FCSTD DOCUMENT  (FreeCAD 1.1R38827 (Git))
Label: composit_stand3_base_part_assembly
License: All rights reserved
LicenseURL: http://en.wikipedia.org/wiki/All_rights_reserved
objects: App::Link×16, PartDesign::CoordinateSystem×3, App::DocumentObjectGroup×3, Part::FeaturePython×3, App::Part×2, App::FeaturePython×1
note: 6 computed .brp shape members not serialized (recipe doc carries the construction recipe); baked Part::Feature solids carry a one-line shape summary decoded from their .brp
EXTERNAL_REF file=composit_stand3_base_part2_model.FCStd obj=Local_CS
EXTERNAL_REF file=composit_stand3_base_part2_model.FCStd obj=Body
EXTERNAL_REF file=composit_stand3_base_part2_model.FCStd obj=Local_CS001
EXTERNAL_REF file=composit_stand3_sink_assembly.FCStd obj=LCS_Origin
EXTERNAL_REF file=composit_stand3_sink_assembly.FCStd obj=Assembly
EXTERNAL_REF file=composit_stand3_base_part2_model.FCStd obj=Local_CS002
EXTERNAL_REF file=composit_stand3_base_part2_model.FCStd obj=Local_CS003
EXTERNAL_REF file=composit_stand3_base_part1_model.FCStd obj=Local_CS
EXTERNAL_REF file=composit_stand3_base_part1_model.FCStd obj=Body
EXTERNAL_REF file=composit_stand3_bottom_shield_model.FCStd obj=Local_CS
EXTERNAL_REF file=composit_stand3_bottom_shield_model.FCStd obj=Body
EXTERNAL_REF file=composit_stand3_base_part1_main.FCStd obj=Join
EXTERNAL_REF file=../module.FCStd obj=Body
EXTERNAL_REF file=composit_stand3_base_part1_model.FCStd obj=Local_CS001
EXTERNAL_REF file=composit_stand3_dropper_fix_assembly.FCStd obj=LCS_Origin
EXTERNAL_REF file=composit_stand3_dropper_fix_assembly.FCStd obj=Assembly
EXTERNAL_REF file=composit_stand3_base_part2_model.FCStd obj=Local_CS004
EXTERNAL_REF file=composit_stand3_base_part2_model.FCStd obj=Local_CS005
EXTERNAL_REF file=composit_stand3_base_part1_main.FCStd obj=Placment
EXTERNAL_REF file=composit_stand3_base_part2_model.FCStd obj=Local_CS006
EXTERNAL_REF file=composit_stand3_top_amplifier_model.FCStd obj=Local_CS
EXTERNAL_REF file=composit_stand3_top_amplifier_model.FCStd obj=Body
EXTERNAL_REF file=composit_stand3_base_part2_model.FCStd obj=Local_CS007
EXTERNAL_REF file=composit_stand3_base_part2_model.FCStd obj=Local_CS008

FEATURE [PartDesign::CoordinateSystem] LCS_Origin
  AttacherType = Attacher::AttachEngine3D
  AttachmentSupport = -> [X_Axis]
  MapMode = 2
FEATURE [App::DocumentObjectGroup] Constraints
FEATURE [App::FeaturePython] Variables  # WARN: FeaturePython — macro-defined, semantics opaque (R4)
  Type = App::PropertyContainer
FEATURE [App::DocumentObjectGroup] Configurations
FEATURE [App::Link] part2
  AttachedBy = #Local_CS
  AttachedTo = Parent Assembly#LCS_Origin
  AttachmentOffset = pos=(0,0,0) rot=(0,0,1;2.0944rad)
  LinkPlacement = pos=(0,0,0) rot=(0,0,1;2.0944rad)
  LinkedObject = -> <external composit_stand3_base_part2_model.FCStd>#Body
  Placement = pos=(0,0,0) rot=(0,0,1;2.0944rad)
  SolverId = Asm4EE
  expr: Placement = LCS_Origin.Placement * AttachmentOffset * composit_stand3_base_part2_model#Local_CS.Placement ^ -1
FEATURE [App::Link] composit_stand3_sink_assembly
  AttachedBy = #LCS_Origin
  AttachedTo = part2#Local_CS001
  LinkPlacement = pos=(-16.7432,7.1e-15,410) rot=(0,0,1;3.14159rad)
  LinkedObject = -> <external composit_stand3_sink_assembly.FCStd>#Assembly
  Placement = pos=(-16.7432,7.1e-15,410) rot=(0,0,1;3.14159rad)
  SolverId = Asm4EE
  expr: Placement = part2.Placement * composit_stand3_base_part2_model#Local_CS001.Placement * AttachmentOffset * composit_stand3_sink_assembly#LCS_Origin.Placement ^ -1
FEATURE [App::Link] composit_stand3_sink_assembly001
  AttachedBy = #LCS_Origin
  AttachedTo = part2#Local_CS002
  LinkPlacement = pos=(8.37158,-14.5,410) rot=(0,0,1;5.23599rad)
  LinkedObject = -> <external composit_stand3_sink_assembly.FCStd>#Assembly
  Placement = pos=(8.37158,-14.5,410) rot=(0,0,1;5.23599rad)
  SolverId = Asm4EE
  expr: Placement = part2.Placement * composit_stand3_base_part2_model#Local_CS002.Placement * AttachmentOffset * composit_stand3_sink_assembly#LCS_Origin.Placement ^ -1
FEATURE [App::Link] composit_stand3_sink_assembly002
  AttachedBy = #LCS_Origin
  AttachedTo = part2#Local_CS003
  LinkPlacement = pos=(8.37158,14.5,410) rot=(0,0,-1;5.23599rad)
  LinkedObject = -> <external composit_stand3_sink_assembly.FCStd>#Assembly
  Placement = pos=(8.37158,14.5,410) rot=(0,0,-1;5.23599rad)
  SolverId = Asm4EE
  expr: Placement = part2.Placement * composit_stand3_base_part2_model#Local_CS003.Placement * AttachmentOffset * composit_stand3_sink_assembly#LCS_Origin.Placement ^ -1
FEATURE [App::Link] part1
  AttachedBy = #Local_CS
  AttachedTo = Parent Assembly#LCS_Origin
  LinkedObject = -> <external composit_stand3_base_part1_model.FCStd>#Body
  SolverId = Asm4EE
  expr: Placement = LCS_Origin.Placement * AttachmentOffset * composit_stand3_base_part1_model#Local_CS.Placement ^ -1
FEATURE [App::Link] bottom_shield
  AttachedBy = #Local_CS
  AttachedTo = Parent Assembly#LCS_Origin
  AttachmentOffset = pos=(0,0,0) rot=(0,0,1;3.14159rad)
  LinkPlacement = pos=(0,0,0) rot=(0,0,1;3.14159rad)
  LinkedObject = -> <external composit_stand3_bottom_shield_model.FCStd>#Body
  Placement = pos=(0,0,0) rot=(0,0,1;3.14159rad)
  SolverId = Asm4EE
  expr: Placement = LCS_Origin.Placement * AttachmentOffset * composit_stand3_bottom_shield_model#Local_CS.Placement ^ -1
FEATURE [App::Link] bottom_shield001
  AttachedBy = #Local_CS
  AttachedTo = Parent Assembly#LCS_Origin
  AttachmentOffset = pos=(0,0,0) rot=(0,0,1;1.0472rad)
  LinkPlacement = pos=(0,0,0) rot=(0,0,1;1.0472rad)
  LinkedObject = -> <external composit_stand3_bottom_shield_model.FCStd>#Body
  Placement = pos=(0,0,0) rot=(0,0,1;1.0472rad)
  SolverId = Asm4EE
  expr: Placement = LCS_Origin.Placement * AttachmentOffset * composit_stand3_bottom_shield_model#Local_CS.Placement ^ -1
FEATURE [App::Link] Link  label="modules_placements"
  LinkedObject = -> <external composit_stand3_base_part1_main.FCStd>#Join
FEATURE [Part::FeaturePython] PolarArray  # WARN: FeaturePython — macro-defined, semantics opaque (R4)
  Alignment = 0
  AttacherType = Attacher::AttachEngine3D
  CellStart = A1
  Count = 3
  DistributionLaw = 0
  EndInclusive = false
  ExposePlacement = false
  FlipX = false
  FlipZ = false
  GeneratorMode = 0
  MarkerShape = 1
  MarkerSize = 200
  NumElements = 3
  OrientMode = 2
  Radius = 0
  Reverse = false
  SpanEnd = 360
  SpanStart = 0
  Step = 120
  Type = lattice2PolarArray2.PolarArray
  UseArcRadius = false
  UseArcRange = 0
  VSGVersion = 1
  Values = 0.0 | 120.0 | 240.0
  ValuesSource = 2
  isLattice = 1
FEATURE [Part::FeaturePython] Populate  label="Populate PolarArray with modules_placements"  # WARN: FeaturePython — macro-defined, semantics opaque (R4)
  Copying = 0
  ExposePlacement = false
  MarkerShape = 1
  MarkerSize = 0
  NumElements = 132
  Object = -> Link
  OutputCompounding = 0
  PlacementsTo = -> PolarArray
  Referencing = 0
  Type = lattice2PopulateCopies.LatticePopulateCopies
  isLattice = 1
FEATURE [App::Link] Link001  label="module_Body"
  LinkedObject = -> <external ../module.FCStd>#Body
FEATURE [Part::FeaturePython] Populate001  label="Populate Populate PolarArray with modules_placements with module_Body"  # WARN: FeaturePython — macro-defined, semantics opaque (R4)
  Copying = 0
  ExposePlacement = false
  MarkerShape = 1
  MarkerSize = 0
  NumElements = 0
  Object = -> Link001
  OutputCompounding = 1
  PlacementsTo = -> Populate
  Referencing = 0
  Type = lattice2PopulateCopies.LatticePopulateCopies
  isLattice = 0
FEATURE [PartDesign::CoordinateSystem] LCS_Origin001
  AttacherType = Attacher::AttachEngine3D
  AttachmentSupport = -> [X_Axis001]
  MapMode = 2
FEATURE [App::Part] Part  label="modules"
  Group = -> [LCS_Origin001,PolarArray,Link001,Link,Populate,Populate001]
  Origin = -> Origin001
FEATURE [App::DocumentObjectGroup] Parts
  Group = -> [Part]
FEATURE [App::Link] modules  label="modules001"
  AttachedBy = #LCS_Origin001
  AttachedTo = Parent Assembly#LCS_Origin
  LinkedObject = -> Part
  SolverId = Asm4EE
  expr: Placement = LCS_Origin.Placement * AttachmentOffset * LCS_Origin001.Placement ^ -1
FEATURE [App::Link] composit_stand3_dropper_fix_assembly
  AttachedBy = #LCS_Origin
  AttachedTo = part1#Local_CS001
  LinkPlacement = pos=(0,0,1428) rot=(0,0,1;0rad)
  LinkedObject = -> <external composit_stand3_dropper_fix_assembly.FCStd>#Assembly
  Placement = pos=(0,0,1428) rot=(0,0,1;0rad)
  SolverId = Asm4EE
  expr: Placement = part1.Placement * composit_stand3_base_part1_model#Local_CS001.Placement * AttachmentOffset * composit_stand3_dropper_fix_assembly#LCS_Origin.Placement ^ -1
FEATURE [App::Link] composit_stand3_dropper_fix_assembly001
  AttachedBy = #LCS_Origin
  AttachedTo = part2#Local_CS004
  LinkPlacement = pos=(0,0,1428) rot=(0,0,1;2.0944rad)
  LinkedObject = -> <external composit_stand3_dropper_fix_assembly.FCStd>#Assembly
  Placement = pos=(0,0,1428) rot=(0,0,1;2.0944rad)
  SolverId = Asm4EE
  expr: Placement = part2.Placement * composit_stand3_base_part2_model#Local_CS004.Placement * AttachmentOffset * composit_stand3_dropper_fix_assembly#LCS_Origin.Placement ^ -1
FEATURE [App::Link] composit_stand3_dropper_fix_1  label="composit_stand3_dropper_fix_assembly002"
  AttachedBy = #LCS_Origin
  AttachedTo = part2#Local_CS005
  LinkPlacement = pos=(0,0,1428) rot=(0,0,1;4.18879rad)
  LinkedObject = -> <external composit_stand3_dropper_fix_assembly.FCStd>#Assembly
  Placement = pos=(0,0,1428) rot=(0,0,1;4.18879rad)
  SolverId = Asm4EE
  expr: Placement = part2.Placement * composit_stand3_base_part2_model#Local_CS005.Placement * AttachmentOffset * composit_stand3_dropper_fix_assembly#LCS_Origin.Placement ^ -1
FEATURE [PartDesign::CoordinateSystem] top_LCS
  AttacherType = Attacher::AttachEngine3D
  AttachmentOffset = pos=(0,0,1434) rot=(0,0,1;0rad)
  AttachmentSupport = -> [XY_Plane]
  MapMode = 5
  Placement = pos=(0,0,1434) rot=(0,0,1;0rad)
  expr: .AttachmentOffset.Base.z = <<composit_stand3_base_part1_main>>#<<top_placement>>.Placement.Base.z + 6 mm
FEATURE [App::Link] top_amplifier
  AttachedBy = #Local_CS
  AttachedTo = part2#Local_CS006
  LinkPlacement = pos=(-13.2791,6.2e-15,1428) rot=(0,0,1;3.14159rad)
  LinkedObject = -> <external composit_stand3_top_amplifier_model.FCStd>#Body
  Placement = pos=(-13.2791,6.2e-15,1428) rot=(0,0,1;3.14159rad)
  SolverId = Asm4EE
  expr: Placement = part2.Placement * composit_stand3_base_part2_model#Local_CS006.Placement * AttachmentOffset * composit_stand3_top_amplifier_model#Local_CS.Placement ^ -1
FEATURE [App::Link] top_amplifier_2
  AttachedBy = #Local_CS
  AttachedTo = part2#Local_CS007
  LinkPlacement = pos=(6.63953,-11.5,1428) rot=(0,0,1;5.23599rad)
  LinkedObject = -> <external composit_stand3_top_amplifier_model.FCStd>#Body
  Placement = pos=(6.63953,-11.5,1428) rot=(0,0,1;5.23599rad)
  SolverId = Asm4EE
  expr: Placement = part2.Placement * composit_stand3_base_part2_model#Local_CS007.Placement * AttachmentOffset * composit_stand3_top_amplifier_model#Local_CS.Placement ^ -1
FEATURE [App::Link] top_amplifier_1
  AttachedBy = #Local_CS
  AttachedTo = part2#Local_CS008
  LinkPlacement = pos=(6.63953,11.5,1428) rot=(0,0,-1;5.23599rad)
  LinkedObject = -> <external composit_stand3_top_amplifier_model.FCStd>#Body
  Placement = pos=(6.63953,11.5,1428) rot=(0,0,-1;5.23599rad)
  SolverId = Asm4EE
  expr: Placement = part2.Placement * composit_stand3_base_part2_model#Local_CS008.Placement * AttachmentOffset * composit_stand3_top_amplifier_model#Local_CS.Placement ^ -1
FEATURE [App::Part] Assembly
  AssemblyType = Part::Link
  Group = -> [LCS_Origin,Constraints,Variables,Configurations,part2,composit_stand3_sink_assembly,composit_stand3_sink_assembly001,composit_stand3_sink_assembly002,part1,bottom_shield,bottom_shield001,modules,composit_stand3_dropper_fix_assembly,composit_stand3_dropper_fix_assembly001,composit_stand3_dropper_fix_1,top_LCS,top_amplifier,top_amplifier_2,top_amplifier_1]
  Origin = -> Origin
  Type = Assembly

RESOLVED EXTERNAL PARTS (link-assembly join: the EXTERNAL_REF files above that resolve inside this repo's crawl, each included once):
---- part ../module.FCStd = doc fcstd_3955753b3a20 ----
FCSTD DOCUMENT  (FreeCAD 1.1R38827 (Git))
Label: module
License: All rights reserved
LicenseURL: http://en.wikipedia.org/wiki/All_rights_reserved
objects: Sketcher::SketchObject×2, Part::Feature×1, PartDesign::FeatureBase×1, PartDesign::Body×1, Spreadsheet::Sheet×1
note: 8 computed .brp shape members not serialized (recipe doc carries the construction recipe); baked Part::Feature solids carry a one-line shape summary decoded from their .brp

FEATURE [Part::Feature] Part__Feature  label="module002"
  shape: bbox 170 x 148 x 41.12 mm, 715 faces (baked)
FEATURE [Sketcher::SketchObject] Sketch  label="module_holes"
  ArcFitTolerance = 0
  FullyConstrained = true
  MakeInternals = false
  sketch-geometry (10):
    g0: LineSegment StartX=59.5 StartY=-3.5 StartZ=0 EndX=59.5 EndY=3.5 EndZ=0
    g1: LineSegment StartX=59.5 StartY=3.5 StartZ=0 EndX=72.5 EndY=3.5 EndZ=0
    g2: LineSegment StartX=72.5 StartY=3.5 StartZ=0 EndX=72.5 EndY=-3.5 EndZ=0
    g3: LineSegment StartX=72.5 StartY=-3.5 StartZ=0 EndX=59.5 EndY=-3.5 EndZ=0
    g4: GeomPoint [constr] X=66 Y=0 Z=0
    g5: LineSegment StartX=-72.5 StartY=-3.5 StartZ=0 EndX=-72.5 EndY=3.5 EndZ=0
    g6: LineSegment StartX=-72.5 StartY=3.5 StartZ=0 EndX=-59.5 EndY=3.5 EndZ=0
    g7: LineSegment StartX=-59.5 StartY=3.5 StartZ=0 EndX=-59.5 EndY=-3.5 EndZ=0
    g8: LineSegment StartX=-59.5 StartY=-3.5 StartZ=0 EndX=-72.5 EndY=-3.5 EndZ=0
    g9: GeomPoint [constr] X=-66 Y=0 Z=0
  constraints (25):
    c: Coincident(g0,g1)
    c: Coincident(g1,g2)
    c: Coincident(g2,g3)
    c: Coincident(g3,g0)
    c: Horizontal(g1)
    c: Horizontal(g3)
    c: Vertical(g0)
    c: Vertical(g2)
    c: Symmetric(g1,g0,g4)
    c: PointOnObject(g4,g-1)
    c: Coincident(g5,g6)
    c: Coincident(g6,g7)
    c: Coincident(g7,g8)
    c: Coincident(g8,g5)
    c: Horizontal(g6)
    c: Horizontal(g8)
    c: Vertical(g5)
    c: Vertical(g7)
    c: Symmetric(g6,g5,g9)
    c: Symmetric(g9,g4,g-2)
    c: Equal(g1,g6)
    c: Equal(g7,g2)
    c: DistanceX(g1,g1) = 13
    c: DistanceY(g2,g2) = 7
    c: DistanceX(g9,g4) = 132
FEATURE [PartDesign::FeatureBase] BaseFeature
  BaseFeature = -> Part__Feature
  Placement = pos=(0,0,0) rot=(0,0,1;1.5708rad)
  Suppressed = false
FEATURE [PartDesign::Body] Body  label="module_Body"
  AllowCompound = false
  BaseFeature = -> Part__Feature
  Group = -> [BaseFeature]
  Origin = -> Origin
  Tip = -> BaseFeature
FEATURE [Spreadsheet::Sheet] Spreadsheet  label="Properties"
  cells = B2(module_width)==148 mm; C2(module_height)==160 mm; D2(module_fixture_distance_x)==132 mm; E2(module_fixture_distance_y)==80 mm; F2(module_hole_x)==13 mm; G2(module_hole_y)==7 mm
FEATURE [Sketcher::SketchObject] Sketch001  label="module_holes001"
  ArcFitTolerance = 0
  FullyConstrained = true
  MakeInternals = false
  sketch-geometry (10):
    g0: LineSegment StartX=59 StartY=-3.5 StartZ=0 EndX=59 EndY=3.5 EndZ=0
    g1: LineSegment StartX=59 StartY=3.5 StartZ=0 EndX=73 EndY=3.5 EndZ=0
    g2: LineSegment StartX=73 StartY=3.5 StartZ=0 EndX=73 EndY=-3.5 EndZ=0
    g3: LineSegment StartX=73 StartY=-3.5 StartZ=0 EndX=59 EndY=-3.5 EndZ=0
    g4: GeomPoint [constr] X=66 Y=0 Z=0
    g5: LineSegment StartX=-73 StartY=-3.5 StartZ=0 EndX=-73 EndY=3.5 EndZ=0
    g6: LineSegment StartX=-73 StartY=3.5 StartZ=0 EndX=-59 EndY=3.5 EndZ=0
    g7: LineSegment StartX=-59 StartY=3.5 StartZ=0 EndX=-59 EndY=-3.5 EndZ=0
    g8: LineSegment StartX=-59 StartY=-3.5 StartZ=0 EndX=-73 EndY=-3.5 EndZ=0
    g9: GeomPoint [constr] X=-66 Y=0 Z=0
  constraints (25):
    c: Coincident(g0,g1)
    c: Coincident(g1,g2)
    c: Coincident(g2,g3)
    c: Coincident(g3,g0)
    c: Horizontal(g1)
    c: Horizontal(g3)
    c: Vertical(g0)
    c: Vertical(g2)
    c: Symmetric(g1,g0,g4)
    c: PointOnObject(g4,g-1)
    c: Coincident(g5,g6)
    c: Coincident(g6,g7)
    c: Coincident(g7,g8)
    c: Coincident(g8,g5)
    c: Horizontal(g6)
    c: Horizontal(g8)
    c: Vertical(g5)
    c: Vertical(g7)
    c: Symmetric(g6,g5,g9)
    c: Symmetric(g9,g4,g-2)
    c: Equal(g1,g6)
    c: Equal(g7,g2)
    c: DistanceX(g1,g1) = 14
    c: DistanceY(g2,g2) = 7
    c: DistanceX(g9,g4) = 132
---- part composit_stand3_base_part1_main.FCStd = doc fcstd_83d21d27950e ----
FCSTD DOCUMENT  (FreeCAD 1.1R38827 (Git))
Label: composit_stand3_base_part1_main
License: All rights reserved
LicenseURL: http://en.wikipedia.org/wiki/All_rights_reserved
objects: Part::FeaturePython×32, Sketcher::SketchObject×7, App::Link×5, Part::Extrusion×3, PartDesign::SubShapeBinder×2, Part::MultiFuse×1, Part::Feature×1
note: 53 computed .brp shape members not serialized (recipe doc carries the construction recipe); baked Part::Feature solids carry a one-line shape summary decoded from their .brp
EXTERNAL_REF file=composit_stand3_main.FCStd obj=Sketch
EXTERNAL_REF file=composit_stand3_main.FCStd obj=LinearArray
EXTERNAL_REF file=../module.FCStd obj=Sketch
EXTERNAL_REF file=composit_stand3_sink_main.FCStd obj=Sketch001
EXTERNAL_REF file=composit_stand3_bottom_shield_main.FCStd obj=Placment
EXTERNAL_REF file=composit_stand3_bottom_shield_main.FCStd obj=LinearArray
EXTERNAL_REF file=composit_stand3_sink_main.FCStd obj=Sketch005

FEATURE [PartDesign::SubShapeBinder] Binder
  BindCopyOnChange = 0
  BindMode = 0
  ClaimChildren = true
  Fuse = false
  MakeFace = false
  OffsetFill = false
  OffsetIntersection = false
  OffsetJoinType = 0
  OffsetOpenResult = false
  PartialLoad = false
  Relative = false
  Support = -> [<external composit_stand3_main.FCStd>#Sketch]
  _Version = 2
FEATURE [Sketcher::SketchObject] Sketch
  ArcFitTolerance = 0
  ExternalGeometry = -> [Binder]
  FullyConstrained = true
  MakeInternals = false
  sketch-geometry (2):
    g0: LineSegment StartX=8.37158 StartY=14.5 StartZ=0 EndX=4.90748 EndY=14.5 EndZ=0
    g1: LineSegment StartX=4.90748 StartY=14.5 StartZ=0 EndX=-2.59252 EndY=27.4904 EndZ=0
  constraints (7):
    c: Horizontal(g0)
    c: Coincident(g0,g1)
    c: Angle(g1) = 2.0944
    c: Coincident(g0,g-3)
    c: Distance(g0,g1) = 3
    c: Distance(g1) = 15
    c: DistanceX(g0) = 4.90748  'x_offset'
FEATURE [Part::FeaturePython] LinearArray  # WARN: FeaturePython — macro-defined, semantics opaque (R4)
  Alignment = 0
  CellStart = A1
  Count = 11
  Dir = (0,0,-1)
  DirIsDriven = true
  DistributionLaw = 0
  DrivenProperty = 1
  EndInclusive = true
  ExposePlacement = false
  GeneratorMode = 1
  MarkerShape = 1
  MarkerSize = 0
  NumElements = 11
  OrientMode = 0
  Point = (0,0,0)
  PointIsDriven = true
  Reverse = false
  SpanEnd = 827
  SpanStart = 27
  Step = 80
  Type = lattice2LinearArray.LinearArray
  VSGVersion = 1
  Values = 27.0 | 107.0 | 187.0 | 267.0 | 347.0 | 427.0 | 507.0 | 587.0 | 667.0 | 747.0 | 827.0
  ValuesSource = 2
  isLattice = 1
  expr: SpanEnd = Step * (Count - 1) * 1 mm + SpanStart
FEATURE [App::Link] Link  label="modules_placement_x"
  LinkTransform = true
  LinkedObject = -> <external composit_stand3_main.FCStd>#LinearArray
FEATURE [Part::FeaturePython] Placment  label="top_placement"  # WARN: FeaturePython — macro-defined, semantics opaque (R4)
  AttacherType = Attacher::AttachEngine3D
  ExposePlacement = true
  MarkerShape = 1
  MarkerSize = 200
  NumElements = 1
  Placement = pos=(0,0,1428) rot=(0,0,1;0rad)
  Type = lattice2AttachablePlacement.AttachablePlacement
  isLattice = 1
FEATURE [Part::FeaturePython] Populate  label="Populate modules_placement_x with LinearArray"  # WARN: FeaturePython — macro-defined, semantics opaque (R4)
  Copying = 0
  ExposePlacement = false
  MarkerShape = 1
  MarkerSize = 0
  NumElements = 22
  Object = -> LinearArray
  OutputCompounding = 0
  PlacementsTo = -> Link
  Referencing = 0
  Type = lattice2PopulateCopies.LatticePopulateCopies
  isLattice = 1
FEATURE [Part::FeaturePython] Populate001  label="Populate Placment with Populate modules_placement_x with LinearArray"  # WARN: FeaturePython — macro-defined, semantics opaque (R4)
  Copying = 0
  ExposePlacement = false
  MarkerShape = 1
  MarkerSize = 0
  NumElements = 22
  Object = -> Populate
  OutputCompounding = 0
  PlacementsTo = -> Placment
  Referencing = 0
  Type = lattice2PopulateCopies.LatticePopulateCopies
  isLattice = 1
FEATURE [Part::FeaturePython] Placment001  # WARN: FeaturePython — macro-defined, semantics opaque (R4)
  AttacherType = Attacher::AttachEngine3D
  ExposePlacement = true
  MarkerShape = 1
  MarkerSize = 50
  NumElements = 1
  Placement = pos=(0,0,0) rot=(0,0.707107,0.707107;3.14159rad)
  Type = lattice2AttachablePlacement.AttachablePlacement
  isLattice = 1
FEATURE [Part::FeaturePython] Populate002  label="Populate Populate Placment with Populate modules_placement_x with LinearArray with Placment001"  # WARN: FeaturePython — macro-defined, semantics opaque (R4)
  Copying = 0
  ExposePlacement = false
  MarkerShape = 1
  MarkerSize = 0
  NumElements = 22
  Object = -> Placment001
  OutputCompounding = 0
  PlacementsTo = -> Populate001
  Referencing = 0
  Type = lattice2PopulateCopies.LatticePopulateCopies
  isLattice = 1
FEATURE [Part::FeaturePython] Placment002  label="sink_placement"  # WARN: FeaturePython — macro-defined, semantics opaque (R4)
  AttacherType = Attacher::AttachEngine3D
  ExposePlacement = true
  MarkerShape = 1
  MarkerSize = 50
  NumElements = 1
  Placement = pos=(8.37158,14.5,410) rot=(0,0,1;1.0472rad)
  Type = lattice2AttachablePlacement.AttachablePlacement
  isLattice = 1
  expr: .Placement.Base.x = <<composit_stand3_main>>#<<main_sketch>>.Constraints.end_width / 2 / tan(60)
  expr: .Placement.Base.y = <<composit_stand3_main>>#<<main_sketch>>.Constraints.end_width / 2
FEATURE [App::Link] Link001  label="module_holes"
  LinkedObject = -> <external ../module.FCStd>#Sketch
FEATURE [Sketcher::SketchObject] Sketch001  label="basin_cut_top_sketch"
  ArcFitTolerance = 0
  FullyConstrained = true
  MakeInternals = false
  Placement = pos=(0,0,400) rot=(1,0,0;1.5708rad)
  expr: .Placement.Base.z = <<basin_cut_sketch>>.Constraints.height
  expr: Constraints[26] = <<basin_cut_sketch>>.Constraints.length
  expr: Constraints[28] = <<composit_stand3_main>>#<<main_sketch>>.Constraints.x_face_offset + 0.5 mm
  expr: Constraints[30] = <<composit_stand3_sink_main>>#<<side_bottom_edge>>.Constraints.angle
  sketch-geometry (14):
    g0: ArcOfEllipse CenterX=8.87158 CenterY=5 CenterZ=0 NormalX=0 NormalY=0 NormalZ=1 MajorRadius=40 MinorRadius=15 AngleXU=1.5708 StartAngle=4.71239 EndAngle=6.28319
    g1: LineSegment [constr] StartX=8.87158 StartY=45 StartZ=0 EndX=8.87158 EndY=-35 EndZ=0
    g2: LineSegment [constr] StartX=-6.12842 StartY=5 StartZ=0 EndX=23.8716 EndY=5 EndZ=0
    g3: GeomPoint [constr] X=8.87158 Y=42.081 Z=0
    g4: GeomPoint [constr] X=8.87158 Y=-32.081 Z=0
    g5: ArcOfCircle CenterX=28.8716 CenterY=5 CenterZ=0 NormalX=0 NormalY=0 NormalZ=1 AngleXU=0 Radius=5 StartAngle=3.14159 EndAngle=4.71239
    g6: LineSegment StartX=28.8716 StartY=0 StartZ=0 EndX=0 EndY=0 EndZ=0
    g7: LineSegment StartX=0 StartY=0 StartZ=0 EndX=0 EndY=45 EndZ=0
    g8: LineSegment StartX=0 StartY=45 StartZ=0 EndX=8.87158 EndY=45 EndZ=0
    g9: LineSegment StartX=238.446 StartY=3.98838 StartZ=0 EndX=238.446 EndY=0 EndZ=0
    g10: LineSegment StartX=238.446 StartY=0 StartZ=0 EndX=170.25 EndY=0 EndZ=0
    g11: LineSegment StartX=170.836 StartY=0.0172058 StartZ=0 EndX=238.446 EndY=3.98838 EndZ=0
    g12: ArcOfCircle CenterX=170.25 CenterY=10 CenterZ=0 NormalX=0 NormalY=0 NormalZ=1 AngleXU=0 Radius=10 StartAngle=4.71239 EndAngle=4.77106
    g13: LineSegment [constr] StartX=0 StartY=0 StartZ=0 EndX=238.446 EndY=14.0056 EndZ=0
  constraints (31):
    c: InternalAlignment(g1-g4 -> g0) x4
    c: Horizontal(g2)
    c: PointOnObject(g5,g-1)
    c: Tangent(g5,g0) = 1.5708
    c: Coincident(g6,g7)
    c: PointOnObject(g7,g-2)
    c: Vertical(g7)
    c: Coincident(g7,g8)
    c: Horizontal(g8)
    c: Tangent(g8,g0) = 1.5708
    c: Radius(g5) = 5
    c: Tangent(g5,g6) = 1.5708
    c: Horizontal(g6)
    c: DistanceY(g7) = 45  'sink_cut_height'
    c: Horizontal(g0,g0)
    c: DistanceX(g2,g2) = 30
    c: PointOnObject(g10,g-1)
    c: Coincident(g11,g9)
    c: PointOnObject(g9,g-1)
    c: Vertical(g9)
    c: Coincident(g9,g10)
    c: Tangent(g12,g10) = 1.5708
    c: Tangent(g12,g11) = -1.5708
    c: DistanceX(g9) = 238.446
    c: Radius(g12) = 10
    c: DistanceX(g0) = 8.87158
    c: Coincident(g13,g6)
    c: Angle(g13) = 0.0586697
    c: Vertical(g9,g13)
    c: Parallel(g11,g13)
    c: Distance(g9,g13) = 10
FEATURE [Part::FeaturePython] Placment003  label="bottom_fix_placement"  # WARN: FeaturePython — macro-defined, semantics opaque (R4)
  AttacherType = Attacher::AttachEngine3D
  AttachmentOffset = pos=(0,0,0) rot=(0,0,1;1.5708rad)
  ExposePlacement = true
  MarkerShape = 1
  MarkerSize = 50
  NumElements = 1
  Placement = pos=(294.4,0,0) rot=(0,0,1;1.5708rad)
  Type = lattice2AttachablePlacement.AttachablePlacement
  isLattice = 1
FEATURE [Sketcher::SketchObject] Sketch002  label="leg_amplifier"
  ArcFitTolerance = 0
  ExternalGeometry = -> [Binder]
  FullyConstrained = true
  MakeInternals = false
  Placement = pos=(238.046,0,0) rot=(0,0,1;0rad)
  expr: .Placement.Base.x = <<basin_cut_sketch>>.Constraints.length - 0.4 mm
  sketch-geometry (5):
    g0: LineSegment StartX=10 StartY=-14.5 StartZ=0 EndX=0 EndY=-14.5 EndZ=0
    g1: LineSegment StartX=0 StartY=-14.5 StartZ=0 EndX=0 EndY=11.5 EndZ=0
    g2: LineSegment StartX=0 StartY=11.5 StartZ=0 EndX=15 EndY=11.5 EndZ=0
    g3: LineSegment [constr] StartX=113.826 StartY=14.5 StartZ=0 EndX=113.826 EndY=0 EndZ=0
    g4: LineSegment [constr] StartX=113.826 StartY=0 StartZ=0 EndX=113.826 EndY=-14.5 EndZ=0
  constraints (16):
    c: Horizontal(g0)
    c: Coincident(g0,g1)
    c: Vertical(g1)
    c: Coincident(g1,g2)
    c: Horizontal(g2)
    c: DistanceY(g1,g-3) = 3
    c: Coincident(g-3,g3)
    c: PointOnObject(g3,g-1)
    c: Vertical(g3)
    c: Coincident(g3,g4)
    c: Vertical(g4)
    c: Equal(g4,g3)
    c: Horizontal(g4,g0)
    c: DistanceX(g2,g2) = 15
    c: DistanceX(g0,g0) = 10
    c: PointOnObject(g-1,g1)
FEATURE [Part::FeaturePython] LinearArray001  # WARN: FeaturePython — macro-defined, semantics opaque (R4)
  Alignment = 0
  CellStart = A1
  Count = 5
  Dir = (1,0,0)
  DirIsDriven = true
  DistributionLaw = 0
  DrivenProperty = 1
  EndInclusive = true
  ExposePlacement = false
  GeneratorMode = 0
  MarkerShape = 1
  MarkerSize = 0
  NumElements = 5
  OrientMode = 1
  Point = (0,0,0)
  PointIsDriven = true
  Reverse = false
  SpanEnd = 50
  SpanStart = 0
  Step = 12.5
  Type = lattice2LinearArray.LinearArray
  VSGVersion = 1
  Values = 0.0 | 12.5 | 25.0 | 37.5 | 50.0
  ValuesSource = 2
  isLattice = 1
FEATURE [Part::FeaturePython] Placment004  # WARN: FeaturePython — macro-defined, semantics opaque (R4)
  AttacherType = Attacher::AttachEngine3D
  AttachmentOffset = pos=(-3,261,7) rot=(-0.57735,-0.57735,0.57735;2.0944rad)
  AttachmentSupport = -> [Sketch]
  ExposePlacement = true
  MapMode = 7
  MarkerShape = 1
  MarkerSize = 5
  NumElements = 1
  Placement = pos=(-1.6906,19.9282,261) rot=(0.250563,-0.935113,0.250563;1.63783rad)
  Type = lattice2AttachablePlacement.AttachablePlacement
  isLattice = 1
FEATURE [Part::FeaturePython] Populate004  label="Populate Placment004 with LinearArray001"  # WARN: FeaturePython — macro-defined, semantics opaque (R4)
  Copying = 0
  ExposePlacement = false
  MarkerShape = 1
  MarkerSize = 0
  NumElements = 5
  Object = -> LinearArray001
  OutputCompounding = 0
  PlacementsTo = -> Placment004
  Referencing = 0
  Type = lattice2PopulateCopies.LatticePopulateCopies
  isLattice = 1
FEATURE [Sketcher::SketchObject] Sketch003  label="basin_cut_sketch"
  ArcFitTolerance = 0
  FullyConstrained = true
  MakeInternals = false
  Placement = pos=(0,0,0) rot=(1,0,0;1.5708rad)
  expr: .Constraints.length = 206.5 / sin(60)
  sketch-geometry (4):
    g0: LineSegment StartX=0 StartY=0 StartZ=0 EndX=238.446 EndY=0 EndZ=0
    g1: LineSegment StartX=238.446 StartY=0 StartZ=0 EndX=238.446 EndY=400 EndZ=0
    g2: LineSegment StartX=238.446 StartY=400 StartZ=0 EndX=0 EndY=400 EndZ=0
    g3: LineSegment StartX=0 StartY=400 StartZ=0 EndX=0 EndY=0 EndZ=0
  constraints (11):
    c: Coincident(g0,g1)
    c: Coincident(g1,g2)
    c: Coincident(g2,g3)
    c: Coincident(g3,g0)
    c: Horizontal(g0)
    c: Horizontal(g2)
    c: Vertical(g1)
    c: Vertical(g3)
    c: Coincident(g0,g-1)
    c: DistanceY(g3,g3) = 400  'height'
    c: DistanceX(g0,g0) = 238.446  'length'
FEATURE [Part::Extrusion] Extrude001
  Base = -> Sketch003
  Dir = (0,-1,2e-16)
  DirMode = 2
  FaceMakerClass = Part::FaceMakerBullseye
  FaceMakerMode = 3
  LengthFwd = 29
  LengthRev = 0
  Solid = true
  Symmetric = true
  expr: LengthFwd = <<composit_stand3_main>>#<<main_sketch>>.Constraints.end_width
FEATURE [Part::Extrusion] Extrude002
  Base = -> Sketch001
  Dir = (0,-1,2e-16)
  DirMode = 2
  FaceMakerClass = Part::FaceMakerBullseye
  FaceMakerMode = 3
  LengthFwd = 29
  LengthRev = 0
  Solid = true
  Symmetric = true
  expr: LengthFwd = <<Extrude001>>.LengthFwd
FEATURE [Part::MultiFuse] Fusion  label="basin_cut"
  Refine = true
  Shapes = -> [Extrude001,Extrude002]
FEATURE [Sketcher::SketchObject] Sketch004
  ArcFitTolerance = 0
  FullyConstrained = true
  MakeInternals = false
  Placement = pos=(8.37158,14.5,0) rot=(0.774597,-0.447214,-0.447214;1.82348rad)
  expr: .Placement.Base.x = composit_stand3_main#<<main_sketch>>.Constraints.x_face_offset
  expr: Constraints[9] = <<basin_cut_sketch>>.Constraints.height + <<basin_cut_top_sketch>>.Constraints.sink_cut_height
  sketch-geometry (4):
    g0: LineSegment StartX=0 StartY=0 StartZ=0 EndX=0 EndY=445 EndZ=0
    g1: LineSegment StartX=0 StartY=445 StartZ=0 EndX=-1 EndY=445 EndZ=0
    g2: LineSegment StartX=-1 StartY=445 StartZ=0 EndX=-1 EndY=0 EndZ=0
    g3: LineSegment StartX=-1 StartY=0 StartZ=0 EndX=0 EndY=0 EndZ=0
  constraints (11):
    c: Coincident(g0,g1)
    c: Coincident(g1,g2)
    c: Coincident(g2,g3)
    c: Coincident(g3,g0)
    c: Vertical(g0)
    c: Vertical(g2)
    c: Horizontal(g1)
    c: Horizontal(g3)
    c: Coincident(g0,g-1)
    c: DistanceY(g0,g0) = 445
    c: DistanceX(g3,g3) = 1
FEATURE [Part::Extrusion] Extrude003
  Base = -> Sketch004
  Dir = (-0.866025,-0.5,2e-16)
  DirMode = 2
  FaceMakerClass = Part::FaceMakerBullseye
  FaceMakerMode = 3
  LengthFwd = 10
  LengthRev = 0
  Solid = true
  Symmetric = false
FEATURE [App::Link] Link002  label="edge_placement"
  LinkTransform = true
  LinkedObject = -> <external composit_stand3_bottom_shield_main.FCStd>#Placment
FEATURE [App::Link] Link003  label="fix_placements"
  LinkTransform = true
  LinkedObject = -> <external composit_stand3_bottom_shield_main.FCStd>#LinearArray
FEATURE [Sketcher::SketchObject] Sketch005  label="shield_fix_hole_sketch"
  ArcFitTolerance = 0
  FullyConstrained = true
  MakeInternals = false
  sketch-geometry (5):
    g0: LineSegment StartX=-3.2 StartY=-26.4022 StartZ=0 EndX=0 EndY=-26.4022 EndZ=0
    g1: LineSegment StartX=0 StartY=-26.4022 StartZ=0 EndX=0 EndY=26.4022 EndZ=0
    g2: LineSegment StartX=0 StartY=26.4022 StartZ=0 EndX=-3.2 EndY=26.4022 EndZ=0
    g3: LineSegment StartX=-3.2 StartY=26.4022 StartZ=0 EndX=-3.2 EndY=-26.4022 EndZ=0
    g4: GeomPoint [constr] X=-1.6 Y=0 Z=0
  constraints (13):
    c: Coincident(g0,g1)
    c: Coincident(g1,g2)
    c: Coincident(g2,g3)
    c: Coincident(g3,g0)
    c: Horizontal(g0)
    c: Horizontal(g2)
    c: Vertical(g1)
    c: Vertical(g3)
    c: Symmetric(g2,g0,g4)
    c: PointOnObject(g4,g-1)
    c: PointOnObject(g1,g-2)
    c: DistanceX(g0,g1) = 3.2
    c: DistanceY(g0,g1) = 52.8044
FEATURE [Part::FeaturePython] Placment005  label="shield_placement"  # WARN: FeaturePython — macro-defined, semantics opaque (R4)
  AttacherType = Attacher::AttachEngine3D
  ExposePlacement = true
  MarkerShape = 1
  MarkerSize = 50
  NumElements = 1
  Placement = pos=(0,0,0) rot=(0,0,1;1.0472rad)
  Type = lattice2AttachablePlacement.AttachablePlacement
  isLattice = 1
FEATURE [Part::FeaturePython] Placment006  label="Custom"  # WARN: FeaturePython — macro-defined, semantics opaque (R4)
  ExposePlacement = true
  FlipZ = false
  Invert = false
  MarkerShape = 1
  MarkerSize = 50
  NumElements = 1
  Placement = pos=(0,0,0) rot=(0.774597,0.447214,0.447214;1.82348rad)
  PlacementChoice = 0
  Type = lattice2Placement.LatticePlacement
  isLattice = 1
FEATURE [Part::FeaturePython] Populate008  label="Populate edge_placement with fix_placements"  # WARN: FeaturePython — macro-defined, semantics opaque (R4)
  Copying = 0
  ExposePlacement = false
  MarkerShape = 1
  MarkerSize = 0
  NumElements = 4
  Object = -> Link003
  OutputCompounding = 0
  PlacementsTo = -> Link002
  Referencing = 0
  Type = lattice2PopulateCopies.LatticePopulateCopies
  isLattice = 1
FEATURE [Part::FeaturePython] Populate009  label="Populate Populate edge_placement with fix_placements with Custom"  # WARN: FeaturePython — macro-defined, semantics opaque (R4)
  Copying = 0
  ExposePlacement = false
  MarkerShape = 1
  MarkerSize = 0
  NumElements = 4
  Object = -> Placment006
  OutputCompounding = 0
  PlacementsTo = -> Populate008
  Referencing = 0
  Type = lattice2PopulateCopies.LatticePopulateCopies
  isLattice = 1
FEATURE [Part::FeaturePython] Mirror002  label="Mirror002 of Populate Populate edge_placement with fix_placements with Custom"  # WARN: FeaturePython — macro-defined, semantics opaque (R4)
  ExposePlacement = false
  FlipX = false
  FlipY = true
  FlipZ = false
  MarkerShape = 1
  MarkerSize = 0
  NumElements = 4
  Object = -> Populate009
  ObjectTraversal = 0
  Type = lattice2Mirror.LatticeMirror
  isLattice = 1
FEATURE [Part::FeaturePython] Populate011  label="Populate shield_placement with Mirror002 of Populate Populate edge_placement with fix_placements with Custom"  # WARN: FeaturePython — macro-defined, semantics opaque (R4)
  Copying = 0
  ExposePlacement = false
  MarkerShape = 1
  MarkerSize = 0
  NumElements = 4
  Object = -> Mirror002
  OutputCompounding = 0
  PlacementsTo = -> Placment005
  Referencing = 0
  Type = lattice2PopulateCopies.LatticePopulateCopies
  isLattice = 1
FEATURE [Part::FeaturePython] Join002  label="shield_fix_holes"  # WARN: FeaturePython — macro-defined, semantics opaque (R4)
  ExposePlacement = false
  Interleave = false
  Links = -> [Populate011]
  MarkerShape = 1
  MarkerSize = 0
  NumElements = 4
  Type = lattice2JoinArrays.JoinArrays
  isLattice = 1
FEATURE [Part::FeaturePython] LinearArray002  label="leg_fix_placements"  # WARN: FeaturePython — macro-defined, semantics opaque (R4)
  Alignment = 0
  CellStart = A1
  Count = 3
  Dir = (1,0,0)
  DirIsDriven = true
  DistributionLaw = 0
  DrivenProperty = 1
  EndInclusive = true
  ExposePlacement = false
  GeneratorMode = 0
  MarkerShape = 1
  MarkerSize = 0
  NumElements = 3
  OrientMode = 1
  Placement = pos=(245,14.5,0) rot=(0.57735,0.57735,0.57735;4.18879rad)
  Point = (0,0,0)
  PointIsDriven = true
  Reverse = false
  SpanEnd = 390
  SpanStart = 20
  Step = 185
  Type = lattice2LinearArray.LinearArray
  VSGVersion = 1
  Values = 20.0 | 205.0 | 390.0
  ValuesSource = 2
  isLattice = 1
  expr: .Placement.Base.y = <<composit_stand3_main>>#<<main_sketch>>.Constraints.end_width / 2
FEATURE [Part::FeaturePython] Placment007  # WARN: FeaturePython — macro-defined, semantics opaque (R4)
  AttacherType = Attacher::AttachEngine3D
  AttachmentOffset = pos=(3,0,4.42) rot=(0.57735,0.57735,0.57735;2.0944rad)
  AttachmentSupport = -> [Sketch]
  ExposePlacement = true
  MapMode = 7
  MarkerShape = 1
  MarkerSize = 20
  NumElements = 1
  Placement = pos=(2.21555,25.1625,0) rot=(0.694747,0.186157,0.694747;3.50969rad)
  Type = lattice2AttachablePlacement.AttachablePlacement
  isLattice = 1
FEATURE [Part::FeaturePython] Placment008  label="magnet_fix_placement"  # WARN: FeaturePython — macro-defined, semantics opaque (R4)
  AttacherType = Attacher::AttachEngine3D
  ExposePlacement = true
  MarkerShape = 1
  MarkerSize = 50
  NumElements = 1
  Placement = pos=(308.872,-14.5,248) rot=(1,0,0;1.5708rad)
  Type = lattice2AttachablePlacement.AttachablePlacement
  isLattice = 1
  expr: .Placement.Base.x = 300.5 mm + <<composit_stand3_main>>#<<main_sketch>>.Constraints.x_face_offset
  expr: .Placement.Base.y = -<<composit_stand3_main>>#<<main_sketch>>.Constraints.end_width / 2
FEATURE [Part::Feature] Body159  label="part1_material_0.30ansi002"
  Placement = pos=(0,0,0) rot=(0,0,-1;1.5708rad)
  shape: bbox 356 x 59.31 x 1428 mm, 498 faces (baked)
FEATURE [Part::FeaturePython] LinearArray003  # WARN: FeaturePython — macro-defined, semantics opaque (R4)
  Alignment = 0
  CellStart = A1
  Count = 5
  Dir = (1,0,0)
  DirIsDriven = true
  DistributionLaw = 0
  DrivenProperty = 1
  EndInclusive = true
  ExposePlacement = false
  GeneratorMode = 0
  MarkerShape = 1
  MarkerSize = 0
  NumElements = 5
  OrientMode = 1
  Point = (0,0,0)
  PointIsDriven = true
  Reverse = false
  SpanEnd = 1343
  SpanStart = 523
  Step = 205
  Type = lattice2LinearArray.LinearArray
  VSGVersion = 1
  Values = 523.0 | 728.0 | 933.0 | 1138.0 | 1343.0
  ValuesSource = 2
  isLattice = 1
FEATURE [Part::FeaturePython] Populate012  label="parts_fix_holes"  # WARN: FeaturePython — macro-defined, semantics opaque (R4)
  Copying = 0
  ExposePlacement = false
  MarkerShape = 1
  MarkerSize = 0
  NumElements = 5
  Object = -> LinearArray003
  OutputCompounding = 0
  PlacementsTo = -> Placment007
  Referencing = 0
  Type = lattice2PopulateCopies.LatticePopulateCopies
  isLattice = 1
FEATURE [Part::FeaturePython] Placment009  # WARN: FeaturePython — macro-defined, semantics opaque (R4)
  AttacherType = Attacher::AttachEngine3D
  ExposePlacement = true
  MarkerShape = 1
  MarkerSize = 20
  NumElements = 1
  Placement = pos=(181.372,0,0) rot=(0,0,1;0rad)
  Type = lattice2AttachablePlacement.AttachablePlacement
  isLattice = 1
  expr: .Placement.Base.x = <<modules_placement_x>>.LinkedObject.Placement.Base.x * 1 mm + (<<modules_placement_x>>.LinkedObject.SpanStart + <<modules_placement_x>>.LinkedObject.SpanEnd) / 2
FEATURE [Part::FeaturePython] PolarArray  # WARN: FeaturePython — macro-defined, semantics opaque (R4)
  Alignment = 0
  AttacherType = Attacher::AttachEngine3D
  CellStart = A1
  Count = 2
  DistributionLaw = 0
  EndInclusive = false
  ExposePlacement = false
  FlipX = false
  FlipZ = false
  GeneratorMode = 0
  MarkerShape = 1
  MarkerSize = 50
  NumElements = 2
  OrientMode = 2
  Radius = 0
  Reverse = false
  SpanEnd = 360
  SpanStart = 0
  Step = 180
  Type = lattice2PolarArray2.PolarArray
  UseArcRadius = false
  UseArcRange = 0
  VSGVersion = 1
  Values = 0.0 | 180.0
  ValuesSource = 2
  isLattice = 1
FEATURE [Part::FeaturePython] Populate013  label="Populate PolarArray with Populate Populate Placment with Populate modules_placement_x with LinearArray with Placment001"  # WARN: FeaturePython — macro-defined, semantics opaque (R4)
  Copying = 0
  ExposePlacement = false
  MarkerShape = 1
  MarkerSize = 0
  NumElements = 44
  Object = -> Populate002
  OutputCompounding = 0
  PlacementsFrom = -> Placment009
  PlacementsTo = -> PolarArray
  Referencing = 3
  Type = lattice2PopulateCopies.LatticePopulateCopies
  isLattice = 1
FEATURE [Part::FeaturePython] Populate014  label="Populate Placment009 with Populate PolarArray with Populate Populate Placment with Populate modules_placement_x with LinearArray with Placment001"  # WARN: FeaturePython — macro-defined, semantics opaque (R4)
  Copying = 0
  ExposePlacement = false
  MarkerShape = 1
  MarkerSize = 0
  NumElements = 44
  Object = -> Populate013
  OutputCompounding = 0
  PlacementsTo = -> Placment009
  Referencing = 0
  Type = lattice2PopulateCopies.LatticePopulateCopies
  isLattice = 1
FEATURE [Part::FeaturePython] Join  label="modules_placements"  # WARN: FeaturePython — macro-defined, semantics opaque (R4)
  ExposePlacement = false
  Interleave = false
  Links = -> [Populate014]
  MarkerShape = 1
  MarkerSize = 0
  NumElements = 44
  Type = lattice2JoinArrays.JoinArrays
  isLattice = 1
FEATURE [App::Link] Link004  label="side_holes_half_sketch"
  LinkTransform = true
  LinkedObject = -> <external composit_stand3_sink_main.FCStd>#Sketch005
FEATURE [PartDesign::SubShapeBinder] Binder001
  BindCopyOnChange = 0
  BindMode = 0
  ClaimChildren = false
  Fuse = false
  MakeFace = true
  OffsetFill = false
  OffsetIntersection = false
  OffsetJoinType = 0
  OffsetOpenResult = false
  PartialLoad = false
  Relative = true
  Support = -> [Link004]
  _Version = 2
FEATURE [Sketcher::SketchObject] Sketch006
  ArcFitTolerance = 1e-06
  ExternalGeometry = -> [Binder001]
  FullyConstrained = true
  MakeInternals = false
  Placement = pos=(0,0,0) rot=(0.774597,0.447214,0.447214;1.82348rad)
  sketch-geometry (6):
    g0: Circle CenterX=13.8756 CenterY=84 CenterZ=0 NormalX=0 NormalY=0 NormalZ=1 AngleXU=0 Radius=1.7
    g1: Circle CenterX=173.002 CenterY=84 CenterZ=0 NormalX=0 NormalY=0 NormalZ=1 AngleXU=0 Radius=1.7
    g2: Circle CenterX=332.128 CenterY=84 CenterZ=0 NormalX=0 NormalY=0 NormalZ=1 AngleXU=0 Radius=1.7
    g3: Circle CenterX=332.128 CenterY=34 CenterZ=0 NormalX=0 NormalY=0 NormalZ=1 AngleXU=0 Radius=1.7
    g4: LineSegment [constr] StartX=13.8756 StartY=84 StartZ=0 EndX=14.3756 EndY=84 EndZ=0
    g5: LineSegment [constr] StartX=331.628 StartY=84 StartZ=0 EndX=332.128 EndY=84 EndZ=0
  constraints (15):
    c: Symmetric(g0,g2,g1)
    c: Horizontal(g0,g2)
    c: Coincident(g4,g0)
    c: Coincident(g4,g-3)
    c: Coincident(g5,g-4)
    c: Coincident(g5,g2)
    c: Equal(g4,g5)
    c: DistanceX(g4,g4) = 0.5
    c: Equal(g3,g2)
    c: Equal(g3,g1)
    c: Equal(g3,g0)
    c: Diameter(g3) = 3.4
    c: Horizontal(g4)
    c: Horizontal(g3,g-5)
    c: Vertical(g3,g2)
FEATURE [Part::FeaturePython] Downgrade  label="Edges of Sketch006"  # WARN: FeaturePython — macro-defined, semantics opaque (R4)
  Base = -> Sketch006
  Mode = 8
FEATURE [Part::FeaturePython] ArrayFromShape  label="Array from Edges of Sketch006"  # WARN: FeaturePython — macro-defined, semantics opaque (R4)
  CompoundTraversal = 1
  ExposePlacement = false
  MarkerShape = 1
  MarkerSize = 20
  NumElements = 4
  OrientElementIndex = 0
  OrientMode = 2
  ShapeLink = -> Downgrade
  TranslateElementIndex = 0
  TranslateMode = 3
  Type = lattice2ArrayFromShape.LatticeArrayFromShape
  isLattice = 1
FEATURE [Part::FeaturePython] Mirror  label="Mirror of Array from Edges of Sketch006"  # WARN: FeaturePython — macro-defined, semantics opaque (R4)
  ExposePlacement = false
  FlipX = false
  FlipY = true
  FlipZ = false
  MarkerShape = 1
  MarkerSize = 0
  NumElements = 4
  Object = -> ArrayFromShape
  ObjectTraversal = 0
  Type = lattice2Mirror.LatticeMirror
  isLattice = 1
FEATURE [Part::FeaturePython] Join003  label="sink_holes"  # WARN: FeaturePython — macro-defined, semantics opaque (R4)
  ExposePlacement = false
  Interleave = false
  Links = -> [ArrayFromShape,Mirror]
  MarkerShape = 1
  MarkerSize = 0
  NumElements = 8
  Type = lattice2JoinArrays.JoinArrays
  isLattice = 1
---- part composit_stand3_base_part1_model.FCStd = doc fcstd_766a5f5e4eff ----
FCSTD DOCUMENT  (FreeCAD 1.1R38827 (Git))
Label: composit_stand3_base_part1_model
License: All rights reserved
LicenseURL: http://en.wikipedia.org/wiki/All_rights_reserved
objects: Part::FeaturePython×10, App::Link×10, PartDesign::SubShapeBinder×7, Part::Extrusion×4, PartDesign::Body×3, PartDesign::CoordinateSystem×3, Part::MultiFuse×3, PartDesign::Boolean×3, Part::Mirroring×2, PartDesign::FeaturePython×2, Sketcher::SketchObject×2, Part::Box×1, Part::Feature×1, Part::Compound×1
note: 49 computed .brp shape members not serialized (recipe doc carries the construction recipe); baked Part::Feature solids carry a one-line shape summary decoded from their .brp
EXTERNAL_REF file=composit_stand3_base_part1_main.FCStd obj=Binder
EXTERNAL_REF file=composit_stand3_base_part1_main.FCStd obj=Sketch
EXTERNAL_REF file=composit_stand3_base_part1_main.FCStd obj=Placment
EXTERNAL_REF file=composit_stand3_base_part1_main.FCStd obj=Placment002
EXTERNAL_REF file=composit_stand3_base_part1_main.FCStd obj=Sketch002
EXTERNAL_REF file=composit_stand3_base_part1_main.FCStd obj=Sketch003
EXTERNAL_REF file=composit_stand3_base_part1_main.FCStd obj=Sketch001
EXTERNAL_REF file=composit_stand3_base_part1_main.FCStd obj=Fusion
EXTERNAL_REF file=composit_stand3_base_part1_main.FCStd obj=Join002
EXTERNAL_REF file=composit_stand3_base_part1_main.FCStd obj=Sketch005
EXTERNAL_REF file=composit_stand3_base_part1_main.FCStd obj=Join
EXTERNAL_REF file=../module.FCStd obj=Sketch
EXTERNAL_REF file=composit_stand3_base_part1_main.FCStd obj=Placment008
EXTERNAL_REF file=composit_stand3_main.FCStd obj=Cylinder001
EXTERNAL_REF file=composit_stand3_base_part1_main.FCStd obj=LinearArray002
EXTERNAL_REF file=composit_stand3_base_part1_main.FCStd obj=Populate012
EXTERNAL_REF file=composit_stand3_base_part1_main.FCStd obj=Join003

FEATURE [PartDesign::SubShapeBinder] Binder
  BindCopyOnChange = 0
  BindMode = 0
  ClaimChildren = true
  Fuse = false
  MakeFace = true
  OffsetFill = false
  OffsetIntersection = false
  OffsetJoinType = 0
  OffsetOpenResult = false
  PartialLoad = false
  Relative = true
  Support = -> [<external composit_stand3_base_part1_main.FCStd>#Sketch,<external composit_stand3_base_part1_main.FCStd>#Binder]
  _Version = 2
  expr: Support = list(<<composit_stand3_base_part1_main>>#Binder._self; <<composit_stand3_base_part1_main>>#Sketch._self)
FEATURE [Part::Mirroring] Part__Mirroring  label="Compound (Mirror #1)"
  Base = (0,0,0)
  Normal = (0,1,0)
  Source = -> Binder
FEATURE [Part::FeaturePython] Connect  # WARN: FeaturePython — macro-defined, semantics opaque (R4)
  Objects = -> [Binder,Part__Mirroring]
  Tolerance = 0
FEATURE [PartDesign::SubShapeBinder] Binder001
  BindCopyOnChange = 0
  BindMode = 0
  ClaimChildren = true
  Context = -> Body [Binder001.]
  Fuse = false
  MakeFace = true
  OffsetFill = false
  OffsetIntersection = false
  OffsetJoinType = 0
  OffsetOpenResult = false
  PartialLoad = false
  Relative = false
  Support = -> [Connect]
  _Version = 2
FEATURE [PartDesign::FeaturePython] BaseBend  # WARN: FeaturePython — macro-defined, semantics opaque (R4)
  BendSide = 0
  BendSketch = -> Binder001
  MidPlane = false
  Reverse = false
  Suppressed = false
  length = 1428
  radius = 0.1
  thickness = 0.3
  expr: length = <<top_placement>>.LinkedObject.Placement.Base.z
FEATURE [PartDesign::Body] Body001
  AllowCompound = false
  Origin = -> Origin001
FEATURE [PartDesign::CoordinateSystem] Local_CS  label="base_LCS"
  AttacherType = Attacher::AttachEngine3D
  AttachmentSupport = -> [XY_Plane]
  MapMode = 5
FEATURE [App::Link] Link001  label="top_placement"
  LinkTransform = true
  LinkedObject = -> <external composit_stand3_base_part1_main.FCStd>#Placment
FEATURE [App::Link] Link002  label="sink_placement"
  LinkTransform = true
  LinkedObject = -> <external composit_stand3_base_part1_main.FCStd>#Placment002
FEATURE [PartDesign::CoordinateSystem] Local_CS001  label="top_LCS"
  AttacherType = Attacher::AttachEngine3D
  AttachmentOffset = pos=(0,0,1428) rot=(0,0,1;0rad)
  AttachmentSupport = -> [XY_Plane]
  MapMode = 5
  Placement = pos=(0,0,1428) rot=(0,0,1;0rad)
  expr: AttachmentOffset = <<top_placement>>.LinkedObject.Placement
FEATURE [PartDesign::CoordinateSystem] Local_CS002  label="sink_LCS"
  AttacherType = Attacher::AttachEngine3D
  AttachmentOffset = pos=(8.37158,14.5,410) rot=(0,0,1;1.0472rad)
  AttachmentSupport = -> [XY_Plane]
  MapMode = 5
  Placement = pos=(8.37158,14.5,410) rot=(0,0,1;1.0472rad)
  expr: AttachmentOffset = <<sink_placement>>.LinkedObject.Placement
FEATURE [Part::Box] Box  label="Cube"
  AttacherType = Attacher::AttachEngine3D
  Height = 74
  Length = 8
  Placement = pos=(-3,-28,1354) rot=(0,0,1;0rad)
  Width = 56
  expr: .Placement.Base.z = <<top_placement>>.LinkedObject.Placement.Base.z * 1 mm - Height
  expr: Width = -.Placement.Base.y * 2
FEATURE [PartDesign::SubShapeBinder] Binder002
  BindCopyOnChange = 0
  BindMode = 0
  ClaimChildren = true
  Fuse = false
  MakeFace = true
  OffsetFill = false
  OffsetIntersection = false
  OffsetJoinType = 0
  OffsetOpenResult = false
  PartialLoad = false
  Placement = pos=(238.046,0,0) rot=(0,0,1;0rad)
  Relative = false
  Support = -> [<external composit_stand3_base_part1_main.FCStd>#Sketch002]
  _Version = 2
  expr: Placement = Support[0][0].Placement
FEATURE [PartDesign::SubShapeBinder] Binder003
  BindCopyOnChange = 0
  BindMode = 0
  ClaimChildren = true
  Context = -> Body002 [Binder003.]
  Fuse = false
  MakeFace = true
  OffsetFill = false
  OffsetIntersection = false
  OffsetJoinType = 0
  OffsetOpenResult = false
  PartialLoad = false
  Placement = pos=(238.046,0,0) rot=(0,0,1;0rad)
  Relative = false
  Support = -> [Binder002]
  _Version = 2
  expr: Placement = Support[0][0].Placement
FEATURE [PartDesign::FeaturePython] BaseBend001  # WARN: FeaturePython — macro-defined, semantics opaque (R4)
  BendSide = 0
  BendSketch = -> Binder003
  MidPlane = false
  Reverse = false
  Suppressed = false
  length = 400
  radius = 0.1
  thickness = 0.3
  expr: length = composit_stand3_base_part1_main#<<basin_cut_sketch>>.Constraints.height
  expr: radius = <<BaseBend>>.radius
  expr: thickness = <<BaseBend>>.thickness
FEATURE [Part::Feature] Body159  label="part1_material_0.30ansi002"
  Placement = pos=(0,0,0) rot=(0,0,-1;1.5708rad)
  shape: bbox 356 x 59.31 x 1428 mm, 498 faces (baked)
FEATURE [PartDesign::SubShapeBinder] Binder004
  BindCopyOnChange = 0
  BindMode = 0
  ClaimChildren = true
  Fuse = false
  MakeFace = true
  OffsetFill = false
  OffsetIntersection = false
  OffsetJoinType = 0
  OffsetOpenResult = false
  PartialLoad = false
  Relative = true
  Support = -> [<external composit_stand3_base_part1_main.FCStd>#Sketch]
  _Version = 2
  expr: Support = <<composit_stand3_base_part1_main>>#Sketch._self
FEATURE [Sketcher::SketchObject] Sketch  label="side_bottom_cut_sketch"
  ArcFitTolerance = 0
  AttachmentOffset = pos=(0,0,0) rot=(0,1,0;1.5708rad)
  AttachmentSupport = -> [Binder004]
  ExternalGeometry = -> [Binder004]
  FullyConstrained = true
  MakeInternals = false
  MapMode = 7
  Placement = pos=(4.90748,14.5,0) rot=(0.377964,0.654654,0.654654;2.41886rad)
  expr: .Constraints.height = <<composit_stand3_base_part1_main>>#<<basin_cut_sketch>>.Constraints.height + <<composit_stand3_base_part1_main>>#<<basin_cut_top_sketch>>.Constraints.sink_cut_height + 55 mm
  sketch-geometry (5):
    g0: LineSegment StartX=0 StartY=0 StartZ=0 EndX=15 EndY=0 EndZ=0
    g1: LineSegment StartX=15 StartY=0 StartZ=0 EndX=15 EndY=505 EndZ=0
    g2: LineSegment StartX=0 StartY=500 StartZ=0 EndX=0 EndY=0 EndZ=0
    g3: LineSegment StartX=10 StartY=500 StartZ=0 EndX=0 EndY=500 EndZ=0
    g4: ArcOfCircle CenterX=10 CenterY=505 CenterZ=0 NormalX=0 NormalY=0 NormalZ=1 AngleXU=0 Radius=5 StartAngle=4.71239 EndAngle=6.28319
  constraints (12):
    c: Coincident(g0,g1)
    c: Coincident(g3,g2)
    c: Coincident(g2,g0)
    c: Vertical(g1)
    c: Vertical(g2)
    c: Coincident(g0,g-1)
    c: Coincident(g0,g-3)
    c: DistanceY(g2,g2) = 500  'height'
    c: Horizontal(g3)
    c: Tangent(g4,g1) = -1.5708
    c: Tangent(g4,g3) = 1.5708
    c: Radius(g4) = 5
FEATURE [Part::Extrusion] Extrude
  Base = -> Sketch
  Dir = (0.866025,0.5,1e-16)
  DirMode = 2
  FaceMakerClass = Part::FaceMakerBullseye
  FaceMakerMode = 3
  LengthFwd = 10
  LengthRev = 0
  Reversed = true
  Solid = true
  Symmetric = false
FEATURE [App::Link] Link003  label="basin_cut"
  LinkedObject = -> <external composit_stand3_base_part1_main.FCStd>#Fusion
FEATURE [App::Link] Link004  label="shield_fix_holes"
  LinkedObject = -> <external composit_stand3_base_part1_main.FCStd>#Join002
FEATURE [PartDesign::SubShapeBinder] Binder005
  BindCopyOnChange = 0
  BindMode = 0
  ClaimChildren = false
  Fuse = false
  MakeFace = true
  OffsetFill = false
  OffsetIntersection = false
  OffsetJoinType = 0
  OffsetOpenResult = false
  PartialLoad = false
  Relative = true
  Support = -> [<external composit_stand3_base_part1_main.FCStd>#Sketch005]
  _Version = 2
FEATURE [Part::Extrusion] Extrude001
  Base = -> Binder005
  Dir = (0,0,1)
  DirMode = 2
  FaceMakerClass = Part::FaceMakerBullseye
  FaceMakerMode = 3
  LengthFwd = 0
  LengthRev = 10
  Solid = false
  Symmetric = false
FEATURE [Part::FeaturePython] Populate  label="Populate Mirror001 of Populate Populate Populate shield_placement with edge_placement with fix_placements with Custom with Extrude001"  # WARN: FeaturePython — macro-defined, semantics opaque (R4)
  Copying = 0
  ExposePlacement = false
  MarkerShape = 1
  MarkerSize = 0
  NumElements = 0
  Object = -> Extrude001
  OutputCompounding = 1
  PlacementsTo = -> Link004
  Referencing = 0
  Type = lattice2PopulateCopies.LatticePopulateCopies
  isLattice = 0
FEATURE [App::Link] Link005  label="modules_placements"
  LinkedObject = -> <external composit_stand3_base_part1_main.FCStd>#Join
FEATURE [PartDesign::SubShapeBinder] Binder006  label="modules_holes_import"
  BindCopyOnChange = 0
  BindMode = 0
  ClaimChildren = false
  Fuse = false
  MakeFace = true
  OffsetFill = false
  OffsetIntersection = false
  OffsetJoinType = 0
  OffsetOpenResult = false
  PartialLoad = false
  Relative = true
  Support = -> [<external ../module.FCStd>#Sketch]
  _Version = 2
FEATURE [Part::Extrusion] Extrude002  label="modules_holes_extrude"
  Base = -> Binder006
  Dir = (0,0,1)
  DirMode = 2
  FaceMakerClass = Part::FaceMakerBullseye
  FaceMakerMode = 3
  LengthFwd = 0
  LengthRev = 10
  Solid = false
  Symmetric = false
FEATURE [Part::FeaturePython] Populate001  label="Populate modules_placements with modules_holes_extrude"  # WARN: FeaturePython — macro-defined, semantics opaque (R4)
  Copying = 0
  ExposePlacement = false
  MarkerShape = 1
  MarkerSize = 0
  NumElements = 0
  Object = -> Extrude002
  OutputCompounding = 1
  PlacementsTo = -> Link005
  Referencing = 0
  Type = lattice2PopulateCopies.LatticePopulateCopies
  isLattice = 0
FEATURE [App::Link] Link  label="magnet_fix_placement"
  LinkClaimChild = true
  LinkTransform = true
  LinkedObject = -> <external composit_stand3_base_part1_main.FCStd>#Placment008
FEATURE [App::Link] Link006  label="hole_3.4mm_rev"
  LinkTransform = true
  LinkedObject = -> <external composit_stand3_main.FCStd>#Cylinder001
FEATURE [App::Link] Link007  label="leg_fix_placements"
  LinkTransform = true
  LinkedObject = -> <external composit_stand3_base_part1_main.FCStd>#LinearArray002
FEATURE [App::Link] Link008  label="parts_fix_holes"
  LinkTransform = true
  LinkedObject = -> <external composit_stand3_base_part1_main.FCStd>#Populate012
FEATURE [Part::FeaturePython] Populate003  label="Populate leg_fix_placements with hole_3.4mm_rev"  # WARN: FeaturePython — macro-defined, semantics opaque (R4)
  Copying = 0
  ExposePlacement = false
  MarkerShape = 1
  MarkerSize = 0
  NumElements = 0
  Object = -> Link006
  OutputCompounding = 1
  PlacementsTo = -> Link007
  Referencing = 0
  Type = lattice2PopulateCopies.LatticePopulateCopies
  isLattice = 0
FEATURE [Part::MultiFuse] Fusion001
  Shapes = -> [Populate003]
FEATURE [PartDesign::Boolean] Boolean002
  BaseFeature = -> BaseBend001
  Group = -> [Fusion001]
  Suppressed = false
  Type = 1
  UsePlacement = true
FEATURE [PartDesign::Body] Body002  label="leg"
  AllowCompound = false
  Group = -> [Binder003,BaseBend001,Boolean002]
  Origin = -> Origin002
  Tip = -> Boolean002
FEATURE [Part::Compound] Compound
  Links = -> [Body002]
FEATURE [Part::FeaturePython] Mirror  label="Mirror of parts_fix_holes"  # WARN: FeaturePython — macro-defined, semantics opaque (R4)
  ExposePlacement = false
  FlipX = false
  FlipY = true
  FlipZ = false
  MarkerShape = 1
  MarkerSize = 0
  NumElements = 5
  Object = -> Link008
  ObjectTraversal = 0
  Type = lattice2Mirror.LatticeMirror
  isLattice = 1
FEATURE [Part::FeaturePython] PolarArray  # WARN: FeaturePython — macro-defined, semantics opaque (R4)
  Alignment = 0
  AttacherType = Attacher::AttachEngine3D
  CellStart = A1
  Count = 2
  DistributionLaw = 0
  EndInclusive = false
  ExposePlacement = false
  FlipX = false
  FlipZ = false
  GeneratorMode = 0
  MarkerShape = 1
  MarkerSize = 10
  NumElements = 2
  OrientMode = 2
  Placement = pos=(0,0,0) rot=(0,0,1;-2.0944rad)
  Radius = 0
  Reverse = false
  SpanEnd = 240
  SpanStart = 0
  Step = 120
  Type = lattice2PolarArray2.PolarArray
  UseArcRadius = false
  UseArcRange = 0
  VSGVersion = 1
  Values = 0.0 | 120.0
  ValuesSource = 2
  isLattice = 1
FEATURE [Part::FeaturePython] Populate004  label="Populate PolarArray with sink_placement"  # WARN: FeaturePython — macro-defined, semantics opaque (R4)
  Copying = 0
  ExposePlacement = false
  MarkerShape = 1
  MarkerSize = 0
  NumElements = 2
  Object = -> Link002
  OutputCompounding = 0
  PlacementsTo = -> PolarArray
  Referencing = 0
  Type = lattice2PopulateCopies.LatticePopulateCopies
  isLattice = 1
FEATURE [Sketcher::SketchObject] Sketch001
  ArcFitTolerance = 0
  AttachmentOffset = pos=(0,0,0) rot=(-0.57735,-0.57735,-0.57735;2.0944rad)
  AttachmentSupport = -> [Binder004]
  FullyConstrained = true
  MakeInternals = false
  MapMode = 7
  Placement = pos=(4.90748,14.5,0) rot=(0,0,1;0rad)
  expr: Constraints[17] = <<BaseBend>>.thickness
  expr: Constraints[6] = <<BaseBend>>.radius
  sketch-geometry (7):
    g0: LineSegment [constr] StartX=0.057735 StartY=0 StartZ=0 EndX=0 EndY=0 EndZ=0
    g1: LineSegment [constr] StartX=0 StartY=0 StartZ=0 EndX=-0.0288675 EndY=0.05 EndZ=0
    g2: ArcOfCircle CenterX=0.057735 CenterY=0.1 CenterZ=0 NormalX=0 NormalY=0 NormalZ=1 AngleXU=0 Radius=0.1 StartAngle=3.66519 EndAngle=4.71239
    g3: LineSegment StartX=0.057735 StartY=0 StartZ=0 EndX=0.057735 EndY=-0.3 EndZ=0
    g4: LineSegment StartX=0.057735 StartY=-0.3 StartZ=0 EndX=-0.173205 EndY=-0.3 EndZ=0
    g5: LineSegment StartX=-0.173205 StartY=-0.3 StartZ=0 EndX=-0.288675 EndY=-0.1 EndZ=0
    g6: LineSegment StartX=-0.288675 StartY=-0.1 StartZ=0 EndX=-0.0288675 EndY=0.05 EndZ=0
  constraints (18):
    c: PointOnObject(g0,g-1)
    c: Coincident(g0,g-1)
    c: Coincident(g0,g1)
    c: Tangent(g2,g1) = 1.5708
    c: Tangent(g2,g0) = 1.5708
    c: Angle(g1) = 2.0944
    c: Radius(g2) = 0.1
    c: Coincident(g0,g3)
    c: Coincident(g3,g4)
    c: Coincident(g4,g5)
    c: Coincident(g5,g6)
    c: Coincident(g6,g1)
    c: Perpendicular(g2,g6)
    c: Perpendicular(g2,g3)
    c: Equal(g6,g3)
    c: Equal(g4,g5)
    c: Perpendicular(g3,g4)
    c: DistanceY(g3,g3) = 0.3
FEATURE [Part::Extrusion] Extrude003
  Base = -> Sketch001
  Dir = (0,0,1)
  DirMode = 2
  FaceMakerClass = Part::FaceMakerBullseye
  FaceMakerMode = 3
  LengthFwd = 500
  LengthRev = 0
  Solid = true
  Symmetric = false
  expr: LengthFwd = <<side_bottom_cut_sketch>>.Constraints.height
FEATURE [Part::MultiFuse] Fusion002
  Shapes = -> [Extrude,Extrude003]
FEATURE [Part::Mirroring] Part__Mirroring001  label="Extrude (Mirror #2)"
  Base = (0,0,0)
  Normal = (0,1,0)
  Source = -> Fusion002
FEATURE [App::Link] Link009  label="sink_holes"
  LinkedObject = -> <external composit_stand3_base_part1_main.FCStd>#Join003
FEATURE [Part::FeaturePython] Populate005  label="Populate Populate PolarArray with sink_placement with sink_holes"  # WARN: FeaturePython — macro-defined, semantics opaque (R4)
  Copying = 0
  ExposePlacement = false
  MarkerShape = 1
  MarkerSize = 0
  NumElements = 16
  Object = -> Link009
  OutputCompounding = 0
  PlacementsTo = -> Populate004
  Referencing = 0
  Type = lattice2PopulateCopies.LatticePopulateCopies
  isLattice = 1
FEATURE [Part::FeaturePython] Join  label="hole_3.4mm_placements"  # WARN: FeaturePython — macro-defined, semantics opaque (R4)
  ExposePlacement = false
  Interleave = false
  Links = -> [Link,Link007,Link008,Mirror,Populate005]
  MarkerShape = 1
  MarkerSize = 10
  NumElements = 30
  Type = lattice2JoinArrays.JoinArrays
  isLattice = 1
FEATURE [Part::FeaturePython] Populate002  label="Populate hole_3.4mm_placements with hole_3.4mm_rev"  # WARN: FeaturePython — macro-defined, semantics opaque (R4)
  Copying = 0
  ExposePlacement = false
  MarkerShape = 1
  MarkerSize = 0
  NumElements = 0
  Object = -> Link006
  OutputCompounding = 1
  PlacementsTo = -> Join
  Referencing = 0
  Type = lattice2PopulateCopies.LatticePopulateCopies
  isLattice = 0
FEATURE [Part::MultiFuse] Fusion
  Shapes = -> [Link003,Box,Part__Mirroring001,Populate,Populate001,Populate002,Fusion002]
FEATURE [PartDesign::Boolean] Boolean
  BaseFeature = -> BaseBend
  Group = -> [Fusion]
  Refine = true
  Suppressed = false
  Type = 1
  UsePlacement = true
FEATURE [PartDesign::Boolean] Boolean001
  BaseFeature = -> Boolean
  Group = -> [Compound]
  Refine = true
  Suppressed = false
  Type = 0
  UsePlacement = true
FEATURE [PartDesign::Body] Body  label="part1"
  AllowCompound = false
  Group = -> [Binder001,BaseBend,Boolean,Boolean001,Local_CS,Local_CS001,Local_CS002]
  Origin = -> Origin
  Tip = -> Boolean
---- part composit_stand3_base_part2_model.FCStd = doc fcstd_e8a079779397 ----
FCSTD DOCUMENT  (FreeCAD 1.1R38827 (Git))
Label: composit_stand3_base_part2_model
License: All rights reserved
LicenseURL: http://en.wikipedia.org/wiki/All_rights_reserved
objects: Part::FeaturePython×20, App::Link×10, PartDesign::CoordinateSystem×9, PartDesign::SubShapeBinder×5, PartDesign::Body×4, Part::MultiFuse×4, PartDesign::Boolean×4, Part::Mirroring×3, PartDesign::FeaturePython×3, Part::Extrusion×3, Part::Compound×1, Part::Cylinder×1, Sketcher::SketchObject×1
note: 66 computed .brp shape members not serialized (recipe doc carries the construction recipe); baked Part::Feature solids carry a one-line shape summary decoded from their .brp
EXTERNAL_REF file=composit_stand3_main.FCStd obj=Sketch
EXTERNAL_REF file=composit_stand3_base_part1_main.FCStd obj=Placment
EXTERNAL_REF file=composit_stand3_base_part1_main.FCStd obj=Placment002
EXTERNAL_REF file=composit_stand3_top_amplifier_main.FCStd obj=Join001
EXTERNAL_REF file=composit_stand3_base_part1_main.FCStd obj=Fusion
EXTERNAL_REF file=composit_stand3_base_part1_main.FCStd obj=Mirror002
EXTERNAL_REF file=composit_stand3_base_part1_main.FCStd obj=Populate009
EXTERNAL_REF file=composit_stand3_base_part1_main.FCStd obj=Sketch005
EXTERNAL_REF file=composit_stand3_base_part1_main.FCStd obj=Join
EXTERNAL_REF file=../module.FCStd obj=Sketch
EXTERNAL_REF file=composit_stand3_base_part1_main.FCStd obj=Placment008
EXTERNAL_REF file=composit_stand3_base_part1_main.FCStd obj=Populate012
EXTERNAL_REF file=composit_stand3_base_part1_main.FCStd obj=Sketch002
EXTERNAL_REF file=composit_stand3_base_part1_main.FCStd obj=LinearArray002

FEATURE [Part::FeaturePython] PolarArray  # WARN: FeaturePython — macro-defined, semantics opaque (R4)
  Alignment = 0
  AttacherType = Attacher::AttachEngine3D
  CellStart = A1
  Count = 2
  DistributionLaw = 0
  EndInclusive = false
  ExposePlacement = false
  FlipX = false
  FlipZ = false
  GeneratorMode = 0
  MarkerShape = 1
  MarkerSize = 10
  NumElements = 2
  OrientMode = 2
  Radius = 0
  Reverse = false
  SpanEnd = 240
  SpanStart = 0
  Step = 120
  Type = lattice2PolarArray2.PolarArray
  UseArcRadius = false
  UseArcRange = 0
  VSGVersion = 1
  Values = 0.0 | 120.0
  ValuesSource = 2
  isLattice = 1
FEATURE [PartDesign::SubShapeBinder] Binder
  BindCopyOnChange = 0
  BindMode = 0
  ClaimChildren = false
  Fuse = false
  MakeFace = true
  OffsetFill = false
  OffsetIntersection = false
  OffsetJoinType = 0
  OffsetOpenResult = false
  PartialLoad = false
  Relative = true
  Support = -> [<external composit_stand3_main.FCStd>#Sketch]
  _Version = 2
FEATURE [Part::Mirroring] Part__Mirroring  label="Binder (Mirror #1)"
  Base = (0,0,0)
  Normal = (0,1,0)
  Source = -> Binder
FEATURE [Part::Compound] Compound
  Links = -> [Binder,Part__Mirroring]
FEATURE [Part::FeaturePython] Populate  label="Populate PolarArray with Compound"  # WARN: FeaturePython — macro-defined, semantics opaque (R4)
  Copying = 0
  ExposePlacement = false
  MarkerShape = 1
  MarkerSize = 0
  NumElements = 0
  Object = -> Compound
  OutputCompounding = 1
  PlacementsTo = -> PolarArray
  Referencing = 0
  Type = lattice2PopulateCopies.LatticePopulateCopies
  isLattice = 0
FEATURE [Part::FeaturePython] Connect  # WARN: FeaturePython — macro-defined, semantics opaque (R4)
  Objects = -> [Populate]
  Tolerance = 0
FEATURE [PartDesign::SubShapeBinder] Binder001
  BindCopyOnChange = 0
  BindMode = 0
  ClaimChildren = true
  Context = -> Body [Binder001.]
  Fuse = false
  MakeFace = true
  OffsetFill = false
  OffsetIntersection = false
  OffsetJoinType = 0
  OffsetOpenResult = false
  PartialLoad = false
  Relative = false
  Support = -> [Connect]
  _Version = 2
FEATURE [PartDesign::FeaturePython] BaseBend  # WARN: FeaturePython — macro-defined, semantics opaque (R4)
  BendSide = 0
  BendSketch = -> Binder001
  MidPlane = false
  Reverse = false
  Suppressed = false
  length = 1428
  radius = 0.1
  thickness = 0.3
  expr: length = composit_stand3_base_part1_main#<<top_placement>>.Placement.Base.z
FEATURE [PartDesign::CoordinateSystem] Local_CS  label="base_LCS"
  AttacherType = Attacher::AttachEngine3D
  AttachmentSupport = -> [XY_Plane]
  MapMode = 5
FEATURE [App::Link] Link  label="sink_placement"
  LinkClaimChild = true
  LinkTransform = true
  LinkedObject = -> <external composit_stand3_base_part1_main.FCStd>#Placment002
FEATURE [PartDesign::CoordinateSystem] Local_CS001  label="sink1_LCS"
  AttacherType = Attacher::AttachEngine3D
  AttachmentOffset = pos=(8.37158,14.5,410) rot=(0,0,1;1.0472rad)
  AttachmentSupport = -> [XY_Plane]
  MapMode = 5
  Placement = pos=(8.37158,14.5,410) rot=(0,0,1;1.0472rad)
  expr: AttachmentOffset = <<sink_placement>>.LinkedObject.Placement
FEATURE [PartDesign::CoordinateSystem] Local_CS002  label="sink2_LCS"
  AttacherType = Attacher::AttachEngine3D
  AttachmentOffset = pos=(-16.7432,7.1e-15,410) rot=(0,0,1;3.14159rad)
  AttachmentSupport = -> [XY_Plane]
  MapMode = 5
  Placement = pos=(-16.7432,7.1e-15,410) rot=(0,0,1;3.14159rad)
  expr: AttachmentOffset = placement(vector(0; 0; 0); rotation(120; 0; 0)) * <<sink1_LCS>>.AttachmentOffset
FEATURE [PartDesign::CoordinateSystem] Local_CS003  label="sink3_LCS"
  AttacherType = Attacher::AttachEngine3D
  AttachmentOffset = pos=(8.37158,-14.5,410) rot=(0,0,1;5.23599rad)
  AttachmentSupport = -> [XY_Plane]
  MapMode = 5
  Placement = pos=(8.37158,-14.5,410) rot=(0,0,1;5.23599rad)
  expr: AttachmentOffset = placement(vector(0; 0; 0); rotation(240; 0; 0)) * <<sink1_LCS>>.AttachmentOffset
FEATURE [Part::FeaturePython] PolarArray001  # WARN: FeaturePython — macro-defined, semantics opaque (R4)
  Alignment = 0
  AttacherType = Attacher::AttachEngine3D
  CellStart = A1
  Count = 3
  DistributionLaw = 0
  EndInclusive = false
  ExposePlacement = false
  FlipX = false
  FlipZ = false
  GeneratorMode = 0
  MarkerShape = 1
  MarkerSize = 0
  NumElements = 3
  OrientMode = 2
  Placement = pos=(0,0,0) rot=(0,0,1;1.0472rad)
  Radius = 13.2791
  Reverse = false
  SpanEnd = 360
  SpanStart = 0
  Step = 120
  Type = lattice2PolarArray2.PolarArray
  UseArcRadius = false
  UseArcRange = 0
  VSGVersion = 1
  Values = 0.0 | 120.0 | 240.0
  ValuesSource = 2
  isLattice = 1
  expr: Radius = <<composit_stand3_main>>#<<main_sketch>>.Constraints.corner_distance - 3 mm / sin(60)
FEATURE [App::Link] Link001  label="top_placement"
  LinkClaimChild = true
  LinkTransform = true
  LinkedObject = -> <external composit_stand3_base_part1_main.FCStd>#Placment
FEATURE [Part::FeaturePython] Populate001  label="Populate top_placement with PolarArray001"  # WARN: FeaturePython — macro-defined, semantics opaque (R4)
  Copying = 0
  ExposePlacement = false
  MarkerShape = 1
  MarkerSize = 0
  NumElements = 3
  Object = -> PolarArray001
  OutputCompounding = 0
  PlacementsTo = -> Link001
  Referencing = 0
  Type = lattice2PopulateCopies.LatticePopulateCopies
  isLattice = 1
FEATURE [App::Link] Link002  label="side_holes"
  LinkedObject = -> <external composit_stand3_top_amplifier_main.FCStd>#Join001
FEATURE [Part::FeaturePython] Populate002  label="Populate Populate top_placement with PolarArray001 with side_holes"  # WARN: FeaturePython — macro-defined, semantics opaque (R4)
  Copying = 0
  ExposePlacement = false
  MarkerShape = 1
  MarkerSize = 0
  NumElements = 18
  Object = -> Link002
  OutputCompounding = 0
  PlacementsTo = -> Populate001
  Referencing = 0
  Type = lattice2PopulateCopies.LatticePopulateCopies
  isLattice = 1
FEATURE [Part::Cylinder] Cylinder  label="hole_3.4mm"
  Angle = 360
  AttacherType = Attacher::AttachEngine3D
  FirstAngle = 0
  Height = 10
  Placement = pos=(0,0,0) rot=(1,0,0;3.14159rad)
  Radius = 2
  SecondAngle = 0
FEATURE [PartDesign::Body] Body001  label="Body"
  AllowCompound = false
  Origin = -> Origin001
FEATURE [App::Link] Link003  label="basin_cut"
  LinkedObject = -> <external composit_stand3_base_part1_main.FCStd>#Fusion
FEATURE [Part::Mirroring] Part__Mirroring001  label="basin_cut (Mirror #2)"
  Base = (0,0,0)
  Normal = (0.866025,-0.5,0)
  Source = -> Link003
  expr: .Normal.x = cos(-30)
  expr: .Normal.y = sin(-30)
FEATURE [App::Link] Link004  label="Mirror002 of Populate Populate edge_placement with fix_placements with Custom"
  LinkedObject = -> <external composit_stand3_base_part1_main.FCStd>#Mirror002
FEATURE [App::Link] Link005  label="Populate Populate edge_placement with fix_placements with Custom"
  LinkedObject = -> <external composit_stand3_base_part1_main.FCStd>#Populate009
FEATURE [Part::FeaturePython] Join  # WARN: FeaturePython — macro-defined, semantics opaque (R4)
  ExposePlacement = false
  Interleave = false
  Links = -> [Link005,Link004]
  MarkerShape = 1
  MarkerSize = 0
  NumElements = 8
  Type = lattice2JoinArrays.JoinArrays
  isLattice = 1
FEATURE [Part::FeaturePython] PolarArray002  # WARN: FeaturePython — macro-defined, semantics opaque (R4)
  Alignment = 0
  AttacherType = Attacher::AttachEngine3D
  CellStart = A1
  Count = 2
  DistributionLaw = 0
  EndInclusive = false
  ExposePlacement = false
  FlipX = false
  FlipZ = false
  GeneratorMode = 0
  MarkerShape = 1
  MarkerSize = 100
  NumElements = 2
  OrientMode = 2
  Placement = pos=(0,0,0) rot=(0,0,-1;1.0472rad)
  Radius = 0
  Reverse = false
  SpanEnd = 240
  SpanStart = 0
  Step = 120
  Type = lattice2PolarArray2.PolarArray
  UseArcRadius = false
  UseArcRange = 0
  VSGVersion = 1
  Values = 0.0 | 120.0
  ValuesSource = 2
  isLattice = 1
FEATURE [Part::FeaturePython] Populate004  label="Populate PolarArray002 with Join"  # WARN: FeaturePython — macro-defined, semantics opaque (R4)
  Copying = 0
  ExposePlacement = false
  MarkerShape = 1
  MarkerSize = 0
  NumElements = 16
  Object = -> Join
  OutputCompounding = 0
  PlacementsTo = -> PolarArray002
  Referencing = 0
  Type = lattice2PopulateCopies.LatticePopulateCopies
  isLattice = 1
FEATURE [PartDesign::SubShapeBinder] Binder002
  BindCopyOnChange = 0
  BindMode = 0
  ClaimChildren = false
  Fuse = false
  MakeFace = true
  OffsetFill = false
  OffsetIntersection = false
  OffsetJoinType = 0
  OffsetOpenResult = false
  PartialLoad = false
  Relative = true
  Support = -> [<external composit_stand3_base_part1_main.FCStd>#Sketch005]
  _Version = 2
FEATURE [Part::Extrusion] Extrude
  Base = -> Binder002
  Dir = (0,0,1)
  DirMode = 2
  FaceMakerClass = Part::FaceMakerBullseye
  FaceMakerMode = 3
  LengthFwd = 0
  LengthRev = 10
  Solid = false
  Symmetric = false
FEATURE [Part::FeaturePython] Populate005  label="Populate Populate PolarArray002 with Join with Extrude"  # WARN: FeaturePython — macro-defined, semantics opaque (R4)
  Copying = 0
  ExposePlacement = false
  MarkerShape = 1
  MarkerSize = 0
  NumElements = 0
  Object = -> Extrude
  OutputCompounding = 1
  PlacementsTo = -> Populate004
  Referencing = 0
  Type = lattice2PopulateCopies.LatticePopulateCopies
  isLattice = 0
FEATURE [App::Link] Link006  label="modules_placements"
  LinkedObject = -> <external composit_stand3_base_part1_main.FCStd>#Join
FEATURE [Part::FeaturePython] Populate006  label="Populate PolarArray with modules_placements"  # WARN: FeaturePython — macro-defined, semantics opaque (R4)
  Copying = 0
  ExposePlacement = false
  MarkerShape = 1
  MarkerSize = 0
  NumElements = 88
  Object = -> Link006
  OutputCompounding = 0
  PlacementsTo = -> PolarArray
  Referencing = 0
  Type = lattice2PopulateCopies.LatticePopulateCopies
  isLattice = 1
FEATURE [PartDesign::SubShapeBinder] Binder003
  BindCopyOnChange = 0
  BindMode = 0
  ClaimChildren = false
  Fuse = false
  MakeFace = true
  OffsetFill = false
  OffsetIntersection = false
  OffsetJoinType = 0
  OffsetOpenResult = false
  PartialLoad = false
  Relative = true
  Support = -> [<external ../module.FCStd>#Sketch]
  _Version = 2
FEATURE [Part::Extrusion] Extrude001
  Base = -> Binder003
  Dir = (0,0,1)
  DirMode = 2
  FaceMakerClass = Part::FaceMakerBullseye
  FaceMakerMode = 3
  LengthFwd = 0
  LengthRev = 10
  Solid = false
  Symmetric = false
FEATURE [Part::FeaturePython] Populate007  label="Populate Populate PolarArray with modules_placements with Extrude001"  # WARN: FeaturePython — macro-defined, semantics opaque (R4)
  Copying = 0
  ExposePlacement = false
  MarkerShape = 1
  MarkerSize = 0
  NumElements = 0
  Object = -> Extrude001
  OutputCompounding = 1
  PlacementsTo = -> Populate006
  Referencing = 0
  Type = lattice2PopulateCopies.LatticePopulateCopies
  isLattice = 0
FEATURE [PartDesign::CoordinateSystem] Local_CS004  label="top_LCS"
  AttacherType = Attacher::AttachEngine3D
  AttachmentOffset = pos=(0,0,1428) rot=(0,0,1;0rad)
  AttachmentSupport = -> [XY_Plane]
  MapMode = 5
  Placement = pos=(0,0,1428) rot=(0,0,1;0rad)
  expr: .AttachmentOffset.Base.z = <<BaseBend>>.length
FEATURE [PartDesign::CoordinateSystem] Local_CS005  label="top_LCS001"
  AttacherType = Attacher::AttachEngine3D
  AttachmentOffset = pos=(0,0,1428) rot=(0,0,1;2.0944rad)
  AttachmentSupport = -> [XY_Plane]
  MapMode = 5
  Placement = pos=(0,0,1428) rot=(0,0,1;2.0944rad)
  expr: .AttachmentOffset.Base.z = <<BaseBend>>.length
FEATURE [Sketcher::SketchObject] Sketch
  ArcFitTolerance = 0
  FullyConstrained = true
  MakeInternals = false
  expr: Constraints[2] = <<composit_stand3_main>>#<<main_sketch>>.Constraints.end_width / 2
  sketch-geometry (4):
    g0: LineSegment [constr] StartX=0 StartY=0 StartZ=0 EndX=8.37158 EndY=14.5 EndZ=0
    g1: LineSegment StartX=8.42931 StartY=14.5 StartZ=0 EndX=8.37158 EndY=14.5 EndZ=0
    g2: LineSegment StartX=8.37158 StartY=14.5 StartZ=0 EndX=8.34271 EndY=14.55 EndZ=0
    g3: ArcOfCircle CenterX=8.42931 CenterY=14.6 CenterZ=0 NormalX=0 NormalY=0 NormalZ=1 AngleXU=0 Radius=0.1 StartAngle=3.66519 EndAngle=4.71239
  constraints (10):
    c: Coincident(g0,g-1)
    c: Angle(g0) = 1.0472
    c: DistanceY(g0) = 14.5
    c: Coincident(g1,g0)
    c: Horizontal(g1)
    c: Coincident(g1,g2)
    c: Angle(g2) = 2.0944
    c: Tangent(g3,g1) = 1.5708
    c: Tangent(g3,g2) = 1.5708
    c: Radius(g3) = 0.1
FEATURE [Part::Extrusion] Extrude002
  Base = -> Sketch
  Dir = (0,0,1)
  DirMode = 2
  FaceMakerClass = Part::FaceMakerBullseye
  FaceMakerMode = 3
  LengthFwd = 445
  LengthRev = 0
  Solid = true
  Symmetric = false
FEATURE [PartDesign::CoordinateSystem] Local_CS006  label="top_amplifier1_LCS"
  AttacherType = Attacher::AttachEngine3D
  AttachmentOffset = pos=(6.63953,11.5,1428) rot=(0,0,1;1.0472rad)
  AttachmentSupport = -> [XY_Plane]
  MapMode = 5
  Placement = pos=(6.63953,11.5,1428) rot=(0,0,1;1.0472rad)
  expr: AttachmentOffset = placement(vector(0; 0; <<BaseBend>>.length); rotation(60; 0; 0)) * placement(vector(<<composit_stand3_main>>#<<main_sketch>>.Constraints.corner_distance - 3 mm / sin(60); 0; 0); rotation(0; 0; 0))
FEATURE [PartDesign::CoordinateSystem] Local_CS007  label="top_amplifier2_LCS"
  AttacherType = Attacher::AttachEngine3D
  AttachmentOffset = pos=(-13.2791,6.2e-15,1428) rot=(0,0,1;3.14159rad)
  AttachmentSupport = -> [XY_Plane]
  MapMode = 5
  Placement = pos=(-13.2791,6.2e-15,1428) rot=(0,0,1;3.14159rad)
  expr: AttachmentOffset = placement(vector(0; 0; 0); rotation(120; 0; 0)) * <<top_amplifier1_LCS>>.AttachmentOffset
FEATURE [PartDesign::CoordinateSystem] Local_CS008  label="top_amplifier3_LCS"
  AttacherType = Attacher::AttachEngine3D
  AttachmentOffset = pos=(6.63953,-11.5,1428) rot=(0,0,1;5.23599rad)
  AttachmentSupport = -> [XY_Plane]
  MapMode = 5
  Placement = pos=(6.63953,-11.5,1428) rot=(0,0,1;5.23599rad)
  expr: AttachmentOffset = placement(vector(0; 0; 0); rotation(240; 0; 0)) * <<top_amplifier1_LCS>>.AttachmentOffset
FEATURE [App::Link] Link007  label="magnet_fix_placement"
  LinkTransform = true
  LinkedObject = -> <external composit_stand3_base_part1_main.FCStd>#Placment008
FEATURE [Part::FeaturePython] Mirror  label="Mirror of magnet_fix_placement"  # WARN: FeaturePython — macro-defined, semantics opaque (R4)
  ExposePlacement = false
  FlipX = false
  FlipY = true
  FlipZ = false
  MarkerShape = 1
  MarkerSize = 50
  NumElements = 1
  Object = -> Link007
  ObjectTraversal = 0
  PivotPlacement = pos=(0,0,0) rot=(0,0,1;1.0472rad)
  Type = lattice2Mirror.LatticeMirror
  isLattice = 1
FEATURE [App::Link] Link008  label="parts_fix_holes"
  LinkedObject = -> <external composit_stand3_base_part1_main.FCStd>#Populate012
FEATURE [Part::FeaturePython] Mirror001  label="Mirror001 of parts_fix_holes"  # WARN: FeaturePython — macro-defined, semantics opaque (R4)
  ExposePlacement = false
  FlipX = false
  FlipY = true
  FlipZ = false
  MarkerShape = 1
  MarkerSize = 0
  NumElements = 5
  Object = -> Link008
  ObjectTraversal = 0
  Type = lattice2Mirror.LatticeMirror
  isLattice = 1
FEATURE [Part::FeaturePython] Join002  # WARN: FeaturePython — macro-defined, semantics opaque (R4)
  ExposePlacement = false
  Interleave = false
  Links = -> [Link008,Mirror001]
  MarkerShape = 1
  MarkerSize = 0
  NumElements = 10
  Placement = pos=(0,0,0) rot=(0,0,1;-2.0944rad)
  Type = lattice2JoinArrays.JoinArrays
  isLattice = 1
FEATURE [PartDesign::SubShapeBinder] Binder004
  BindCopyOnChange = 0
  BindMode = 0
  ClaimChildren = false
  Fuse = false
  MakeFace = true
  OffsetFill = false
  OffsetIntersection = false
  OffsetJoinType = 0
  OffsetOpenResult = false
  PartialLoad = false
  Relative = true
  Support = -> [<external composit_stand3_base_part1_main.FCStd>#Sketch002]
  _Version = 2
FEATURE [Part::Mirroring] Part__Mirroring002  label="Binder004 (Mirror #3)"
  Base = (0,0,0)
  Normal = (0.866025,-0.5,0)
  Source = -> Binder004
  expr: .Normal.x = cos(-30)
  expr: .Normal.y = sin(-30)
FEATURE [PartDesign::FeaturePython] BaseBend001  # WARN: FeaturePython — macro-defined, semantics opaque (R4)
  BendSide = 0
  BendSketch = -> Binder004
  MidPlane = false
  Reverse = false
  Suppressed = false
  length = 400
  radius = 0.1
  thickness = 0.3
  expr: radius = <<BaseBend>>.radius
  expr: thickness = <<BaseBend>>.thickness
FEATURE [PartDesign::FeaturePython] BaseBend002  # WARN: FeaturePython — macro-defined, semantics opaque (R4)
  BendSide = 1
  BendSketch = -> Part__Mirroring002
  MidPlane = false
  Reverse = false
  Suppressed = false
  length = 400
  radius = 0.1
  thickness = 0.3
  expr: length = <<BaseBend001>>.length
  expr: radius = <<BaseBend>>.radius
  expr: thickness = <<BaseBend>>.thickness
FEATURE [App::Link] Link009  label="leg_fix_placements"
  LinkTransform = true
  LinkedObject = -> <external composit_stand3_base_part1_main.FCStd>#LinearArray002
FEATURE [Part::FeaturePython] Mirror002  label="Mirror002 of leg_fix_placements"  # WARN: FeaturePython — macro-defined, semantics opaque (R4)
  ExposePlacement = false
  FlipX = true
  FlipY = false
  FlipZ = false
  MarkerShape = 1
  MarkerSize = 0
  NumElements = 3
  Object = -> Link009
  ObjectTraversal = 0
  PivotPlacement = pos=(0,0,0) rot=(0,0,1;-0.523599rad)
  Type = lattice2Mirror.LatticeMirror
  isLattice = 1
FEATURE [Part::FeaturePython] Join001  label="hole_3.4mm_placements"  # WARN: FeaturePython — macro-defined, semantics opaque (R4)
  ExposePlacement = false
  Interleave = false
  Links = -> [Populate002,Mirror,Join002,Link009,Mirror002]
  MarkerShape = 1
  MarkerSize = 0
  NumElements = 35
  Type = lattice2JoinArrays.JoinArrays
  isLattice = 1
FEATURE [Part::FeaturePython] Populate003  label="Populate Populate Populate top_placement with PolarArray001 with side_holes with hole_3.4mm"  # WARN: FeaturePython — macro-defined, semantics opaque (R4)
  Copying = 0
  ExposePlacement = false
  MarkerShape = 1
  MarkerSize = 0
  NumElements = 0
  Object = -> Cylinder
  OutputCompounding = 1
  PlacementsTo = -> Join001
  Referencing = 0
  Type = lattice2PopulateCopies.LatticePopulateCopies
  isLattice = 0
FEATURE [Part::MultiFuse] Fusion
  Refine = true
  Shapes = -> [Populate003,Populate005,Populate007,Link003,Part__Mirroring001,Extrude002]
FEATURE [PartDesign::Boolean] Boolean
  BaseFeature = -> BaseBend
  Group = -> [Fusion]
  Refine = true
  Suppressed = false
  Type = 1
  UsePlacement = true
FEATURE [Part::FeaturePython] Populate008  label="Populate leg_fix_placements with hole_3.4mm"  # WARN: FeaturePython — macro-defined, semantics opaque (R4)
  Copying = 0
  ExposePlacement = false
  MarkerShape = 1
  MarkerSize = 0
  NumElements = 0
  Object = -> Cylinder
  OutputCompounding = 1
  PlacementsTo = -> Link009
  Referencing = 0
  Type = lattice2PopulateCopies.LatticePopulateCopies
  isLattice = 0
FEATURE [Part::FeaturePython] Populate009  label="Populate Mirror002 of leg_fix_placements with hole_3.4mm"  # WARN: FeaturePython — macro-defined, semantics opaque (R4)
  Copying = 0
  ExposePlacement = false
  MarkerShape = 1
  MarkerSize = 0
  NumElements = 0
  Object = -> Cylinder
  OutputCompounding = 1
  PlacementsTo = -> Mirror002
  Referencing = 0
  Type = lattice2PopulateCopies.LatticePopulateCopies
  isLattice = 0
FEATURE [Part::MultiFuse] Fusion001
  Shapes = -> [Populate008]
FEATURE [PartDesign::Boolean] Boolean001
  BaseFeature = -> BaseBend001
  Group = -> [Fusion001]
  Suppressed = false
  Type = 1
  UsePlacement = true
FEATURE [PartDesign::Body] Body002
  AllowCompound = false
  Group = -> [BaseBend001,Boolean001]
  Origin = -> Origin002
  Tip = -> Boolean001
FEATURE [Part::MultiFuse] Fusion002
  Shapes = -> [Populate009]
FEATURE [PartDesign::Boolean] Boolean002
  BaseFeature = -> BaseBend002
  Group = -> [Fusion002]
  Suppressed = false
  Type = 1
  UsePlacement = true
FEATURE [PartDesign::Body] Body003
  AllowCompound = false
  Group = -> [BaseBend002,Boolean002]
  Origin = -> Origin003
  Tip = -> Boolean002
FEATURE [Part::MultiFuse] Fusion003
  Shapes = -> [Body002,Body003]
FEATURE [PartDesign::Boolean] Boolean003
  BaseFeature = -> Boolean
  Group = -> [Fusion003]
  Refine = true
  Suppressed = false
  Type = 0
  UsePlacement = true
FEATURE [PartDesign::Body] Body  label="part2"
  AllowCompound = false
  Group = -> [Binder001,BaseBend,Local_CS,Local_CS001,Local_CS002,Local_CS003,Boolean,Local_CS004,Local_CS005,Local_CS006,Local_CS007,Local_CS008,Boolean003]
  Origin = -> Origin
  Tip = -> Boolean003
---- part composit_stand3_bottom_shield_model.FCStd = doc fcstd_e70fc0dd8a42 ----
FCSTD DOCUMENT  (FreeCAD 1.1R38827 (Git))
Label: composit_stand3_bottom_shield_model
License: All rights reserved
LicenseURL: http://en.wikipedia.org/wiki/All_rights_reserved
objects: Part::FeaturePython×15, PartDesign::SubShapeBinder×3, PartDesign::FeaturePython×2, PartDesign::Body×2, App::Link×2, Part::Feature×2, Part::MultiFuse×2, PartDesign::Boolean×2, Part::Mirroring×1, Part::Extrusion×1, Part::Cylinder×1, Sketcher::SketchObject×1, PartDesign::CoordinateSystem×1
note: 38 computed .brp shape members not serialized (recipe doc carries the construction recipe); baked Part::Feature solids carry a one-line shape summary decoded from their .brp
EXTERNAL_REF file=composit_stand3_bottom_shield_main.FCStd obj=Sketch
EXTERNAL_REF file=composit_stand3_bottom_shield_main.FCStd obj=Sketch001
EXTERNAL_REF file=composit_stand3_bottom_shield_main.FCStd obj=LinearArray
EXTERNAL_REF file=composit_stand3_bottom_shield_main.FCStd obj=Placment

FEATURE [PartDesign::SubShapeBinder] Binder
  BindCopyOnChange = 0
  BindMode = 0
  ClaimChildren = true
  Fuse = false
  MakeFace = true
  OffsetFill = false
  OffsetIntersection = false
  OffsetJoinType = 0
  OffsetOpenResult = false
  PartialLoad = false
  Relative = false
  Support = -> [<external composit_stand3_bottom_shield_main.FCStd>#Sketch]
  _Version = 2
FEATURE [PartDesign::SubShapeBinder] Binder001
  BindCopyOnChange = 0
  BindMode = 0
  ClaimChildren = true
  Context = -> Body [Binder001.]
  Fuse = false
  MakeFace = true
  OffsetFill = false
  OffsetIntersection = false
  OffsetJoinType = 0
  OffsetOpenResult = false
  PartialLoad = false
  Relative = false
  Support = -> [Sketch]
  _Version = 2
FEATURE [PartDesign::FeaturePython] BaseBend  # WARN: FeaturePython — macro-defined, semantics opaque (R4)
  BendSide = 0
  BendSketch = -> Binder001
  MidPlane = false
  Reverse = false
  Suppressed = false
  length = 425
  radius = 779.545
  thickness = 1.5
  expr: radius = composit_stand3_bottom_shield_main#<<main_sketch>>.Constraints.r - 5 mm
FEATURE [PartDesign::Body] Body001
  AllowCompound = false
  Origin = -> Origin001
FEATURE [PartDesign::SubShapeBinder] Binder002
  BindCopyOnChange = 0
  BindMode = 0
  ClaimChildren = true
  Fuse = false
  MakeFace = true
  OffsetFill = false
  OffsetIntersection = false
  OffsetJoinType = 0
  OffsetOpenResult = false
  PartialLoad = false
  Relative = false
  Support = -> [<external composit_stand3_bottom_shield_main.FCStd>#Sketch001]
  _Version = 2
FEATURE [Part::Mirroring] Part__Mirroring001  label="Binder002 (Mirror #2)"
  Base = (0,0,0)
  Normal = (0,1,0)
  Source = -> Binder002
FEATURE [Part::FeaturePython] Connect001  # WARN: FeaturePython — macro-defined, semantics opaque (R4)
  Objects = -> [Binder002,Part__Mirroring001]
  Tolerance = 0
FEATURE [Part::Extrusion] Extrude
  Base = -> Connect001
  Dir = (0,0,1)
  DirMode = 2
  FaceMakerClass = Part::FaceMakerBullseye
  FaceMakerMode = 3
  LengthFwd = 1.5
  LengthRev = 0
  Solid = true
  Symmetric = false
  expr: LengthFwd = <<BaseBend>>.thickness
FEATURE [App::Link] Link  label="fix_placements"
  LinkedObject = -> <external composit_stand3_bottom_shield_main.FCStd>#LinearArray
FEATURE [Part::FeaturePython] Placment001  # WARN: FeaturePython — macro-defined, semantics opaque (R4)
  AttacherType = Attacher::AttachEngine3D
  ExposePlacement = true
  MarkerShape = 1
  MarkerSize = 50
  NumElements = 1
  Placement = pos=(0,0,0) rot=(-0.435046,-0.636685,0.636685;2.32089rad)
  Type = lattice2AttachablePlacement.AttachablePlacement
  isLattice = 1
  expr: .Placement.Rotation.Yaw = composit_stand3_bottom_shield_main#Sketch.Constraints.angle
FEATURE [Part::Cylinder] Cylinder  label="fix_cyl"
  Angle = 360
  AttacherType = Attacher::AttachEngine3D
  FirstAngle = 0
  Height = 10
  Radius = 2
  SecondAngle = 0
FEATURE [Part::FeaturePython] LinearArray  # WARN: FeaturePython — macro-defined, semantics opaque (R4)
  Alignment = 0
  CellStart = A1
  Count = 2
  Dir = (0,0,1)
  DirIsDriven = true
  DistributionLaw = 0
  DrivenProperty = 1
  EndInclusive = true
  ExposePlacement = false
  GeneratorMode = 0
  MarkerShape = 1
  MarkerSize = 0
  NumElements = 2
  OrientMode = 0
  Point = (0,0,0)
  PointIsDriven = true
  Reverse = false
  SpanEnd = 390
  SpanStart = 35
  Step = 355
  Type = lattice2LinearArray.LinearArray
  VSGVersion = 1
  Values = 35.0 | 390.0
  ValuesSource = 2
  isLattice = 1
  expr: SpanEnd = <<fix_placements>>.SpanEnd
  expr: SpanStart = <<fix_placements>>.SpanStart
FEATURE [Part::FeaturePython] Placment002  # WARN: FeaturePython — macro-defined, semantics opaque (R4)
  AttacherType = Attacher::AttachEngine3D
  AttachmentOffset = pos=(5.5,0,0) rot=(0,0,1;0rad)
  AttachmentSupport = -> [Placment001]
  ExposePlacement = true
  MapMode = 2
  MarkerShape = 1
  MarkerSize = 10
  NumElements = 1
  Placement = pos=(-1.99881,5.12394,-3e-16) rot=(0.435046,0.636685,-0.636685;3.96229rad)
  Type = lattice2AttachablePlacement.AttachablePlacement
  isLattice = 1
FEATURE [Part::FeaturePython] Populate003  label="Populate LinearArray with Placment002"  # WARN: FeaturePython — macro-defined, semantics opaque (R4)
  Copying = 0
  ExposePlacement = false
  MarkerShape = 1
  MarkerSize = 0
  NumElements = 2
  Object = -> Placment002
  OutputCompounding = 0
  PlacementsTo = -> LinearArray
  Referencing = 0
  Type = lattice2PopulateCopies.LatticePopulateCopies
  isLattice = 1
FEATURE [Sketcher::SketchObject] Sketch
  ArcFitTolerance = 0
  ExternalGeometry = -> [Binder]
  FullyConstrained = true
  MakeInternals = false
  expr: Constraints[3] = composit_stand3_bottom_shield_main#<<main_sketch>>.Constraints.angle - 180 deg
  sketch-geometry (2):
    g0: LineSegment StartX=181.794 StartY=283.998 StartZ=0 EndX=292.58 EndY=0 EndZ=0
    g1: LineSegment StartX=292.58 StartY=0 StartZ=0 EndX=181.794 EndY=-283.998 EndZ=0
  constraints (5):
    c: Coincident(g0,g1)
    c: Symmetric(g1,g0,g-1)
    c: PointOnObject(g0,g-1)
    c: Angle(g0) = -1.19886
    c: Coincident(g0,g-3)
FEATURE [PartDesign::CoordinateSystem] Local_CS  label="base_LCS"
  AttacherType = Attacher::AttachEngine3D
  AttachmentSupport = -> [XY_Plane]
  MapMode = 5
FEATURE [Part::Feature] Link008  label="sector_plexiglass_material_0.30ansi001"
  Placement = pos=(0,0,0) rot=(0,0,1;1.5708rad)
  shape: bbox 58.56 x 590.7 x 425 mm, 70 faces (baked)
FEATURE [App::Link] Link009  label="edge_placement"
  LinkTransform = true
  LinkedObject = -> <external composit_stand3_bottom_shield_main.FCStd>#Placment
FEATURE [Part::FeaturePython] Populate004  label="Populate Placment with Populate LinearArray with Placment002"  # WARN: FeaturePython — macro-defined, semantics opaque (R4)
  Copying = 0
  ExposePlacement = false
  MarkerShape = 1
  MarkerSize = 0
  NumElements = 2
  Object = -> Populate003
  OutputCompounding = 0
  PlacementsTo = -> Link009
  Referencing = 0
  Type = lattice2PopulateCopies.LatticePopulateCopies
  isLattice = 1
FEATURE [Part::FeaturePython] Mirror001  label="Mirror001 of Populate Placment with Populate LinearArray with Placment002"  # WARN: FeaturePython — macro-defined, semantics opaque (R4)
  ExposePlacement = false
  FlipX = false
  FlipY = true
  FlipZ = false
  MarkerShape = 1
  MarkerSize = 0
  NumElements = 2
  Object = -> Populate004
  ObjectTraversal = 0
  Type = lattice2Mirror.LatticeMirror
  isLattice = 1
FEATURE [Part::FeaturePython] Join001  # WARN: FeaturePython — macro-defined, semantics opaque (R4)
  ExposePlacement = false
  Interleave = false
  Links = -> [Populate004,Mirror001]
  MarkerShape = 1
  MarkerSize = 0
  NumElements = 4
  Type = lattice2JoinArrays.JoinArrays
  isLattice = 1
FEATURE [Part::FeaturePython] Populate005  label="Populate Join001 with fix_cyl"  # WARN: FeaturePython — macro-defined, semantics opaque (R4)
  Copying = 0
  ExposePlacement = false
  MarkerShape = 1
  MarkerSize = 0
  NumElements = 0
  Object = -> Cylinder
  OutputCompounding = 1
  PlacementsTo = -> Join001
  Referencing = 0
  Type = lattice2PopulateCopies.LatticePopulateCopies
  isLattice = 0
FEATURE [Part::MultiFuse] Fusion001
  Shapes = -> [Populate005]
FEATURE [Part::Feature] Body002  label="bottom_shield001"
  shape: bbox 67.07 x 590.7 x 425 mm, 66 faces (baked)
FEATURE [Part::FeaturePython] Placment  # WARN: FeaturePython — macro-defined, semantics opaque (R4)
  AttacherType = Attacher::AttachEngine3D
  AttachmentSupport = -> [Binder]
  ExposePlacement = true
  MapMode = 1
  MarkerShape = 1
  MarkerSize = 50
  NumElements = 1
  Placement = pos=(181.794,283.998,0) rot=(0,0,1;0rad)
  Type = lattice2AttachablePlacement.AttachablePlacement
  isLattice = 1
FEATURE [Part::FeaturePython] Populate  label="Populate Placment with fix_placements"  # WARN: FeaturePython — macro-defined, semantics opaque (R4)
  Copying = 0
  ExposePlacement = false
  MarkerShape = 1
  MarkerSize = 0
  NumElements = 4
  Object = -> Link
  OutputCompounding = 0
  PlacementsTo = -> Placment
  Referencing = 0
  Type = lattice2PopulateCopies.LatticePopulateCopies
  isLattice = 1
FEATURE [Part::FeaturePython] Populate001  label="Populate Populate Placment with fix_placements with Placment001"  # WARN: FeaturePython — macro-defined, semantics opaque (R4)
  Copying = 0
  ExposePlacement = false
  MarkerShape = 1
  MarkerSize = 0
  NumElements = 4
  Object = -> Placment001
  OutputCompounding = 0
  PlacementsTo = -> Populate
  Referencing = 0
  Type = lattice2PopulateCopies.LatticePopulateCopies
  isLattice = 1
FEATURE [Part::FeaturePython] Mirror  label="Mirror of Populate Populate Placment with fix_placements with Placment001"  # WARN: FeaturePython — macro-defined, semantics opaque (R4)
  ExposePlacement = false
  FlipX = false
  FlipY = true
  FlipZ = false
  MarkerShape = 1
  MarkerSize = 0
  NumElements = 4
  Object = -> Populate001
  ObjectTraversal = 0
  Type = lattice2Mirror.LatticeMirror
  isLattice = 1
FEATURE [Part::FeaturePython] Join  # WARN: FeaturePython — macro-defined, semantics opaque (R4)
  ExposePlacement = false
  Interleave = false
  Links = -> [Populate001,Mirror]
  MarkerShape = 1
  MarkerSize = 0
  NumElements = 8
  Type = lattice2JoinArrays.JoinArrays
  isLattice = 1
FEATURE [Part::FeaturePython] Populate002  label="Populate Populate Populate Placment with fix_placements with Placment001 with Extrude"  # WARN: FeaturePython — macro-defined, semantics opaque (R4)
  Copying = 0
  ExposePlacement = false
  MarkerShape = 1
  MarkerSize = 0
  NumElements = 0
  Object = -> Extrude
  OutputCompounding = 1
  PlacementsTo = -> Join
  Referencing = 0
  Type = lattice2PopulateCopies.LatticePopulateCopies
  isLattice = 0
FEATURE [Part::MultiFuse] Fusion
  Shapes = -> [Populate002]
FEATURE [PartDesign::Boolean] Boolean
  BaseFeature = -> BaseBend
  Group = -> [Fusion]
  Suppressed = false
  Type = 0
  UsePlacement = true
FEATURE [PartDesign::Boolean] Boolean001
  BaseFeature = -> Boolean
  Group = -> [Fusion001]
  Suppressed = false
  Type = 1
  UsePlacement = true
FEATURE [PartDesign::FeaturePython] Extend  # WARN: FeaturePython — macro-defined, semantics opaque (R4)
  BaseFeature = -> Boolean001
  Offset = 0.02
  Refine = true
  Suppressed = false
  UseSubtraction = false
  baseObject = -> Boolean001 [Face1]
  gap1 = 0
  gap2 = 0
  length = 0
FEATURE [PartDesign::Body] Body  label="bottom_shield"
  AllowCompound = false
  Group = -> [Binder001,BaseBend,Boolean,Boolean001,Extend,Local_CS]
  Origin = -> Origin
  Tip = -> Extend
---- part composit_stand3_dropper_fix_assembly.FCStd = doc fcstd_2bbee5c5b194 ----
FCSTD DOCUMENT  (FreeCAD 1.1R38827 (Git))
Label: composit_stand3_dropper_fix_assembly
License: All rights reserved
LicenseURL: http://en.wikipedia.org/wiki/All_rights_reserved
objects: App::Link×10, PartDesign::CoordinateSystem×2, App::Part×2, Part::Compound×1, Part::FeaturePython×1, App::DocumentObjectGroup×1
note: 4 computed .brp shape members not serialized (recipe doc carries the construction recipe); baked Part::Feature solids carry a one-line shape summary decoded from their .brp
EXTERNAL_REF file=composit_stand3_dropper_fix_bottom_model.FCStd obj=Local_CS
EXTERNAL_REF file=composit_stand3_dropper_fix_bottom_model.FCStd obj=Body
EXTERNAL_REF file=composit_stand3_dropper_fix_top_model.FCStd obj=Local_CS
EXTERNAL_REF file=composit_stand3_dropper_fix_top_model.FCStd obj=Body
EXTERNAL_REF file=composit_stand3_dropper_fix_fixture_model.FCStd obj=Local_CS
EXTERNAL_REF file=composit_stand3_dropper_fix_fixture_model.FCStd obj=Body
EXTERNAL_REF file=composit_stand3_dropper_fix_cap_outer_model.FCStd obj=Local_CS
EXTERNAL_REF file=composit_stand3_dropper_fix_cap_outer_model.FCStd obj=Body
EXTERNAL_REF file=composit_stand3_dropper_fix_cap_inner_model.FCStd obj=Local_CS
EXTERNAL_REF file=composit_stand3_dropper_fix_cap_inner_model.FCStd obj=Body
EXTERNAL_REF file=composit_stand3_dropper_fix_cap_inner_model.FCStd obj=Local_CS001
EXTERNAL_REF file=composit_stand3_dropper_fix_cap_inner_model.FCStd obj=Body001
EXTERNAL_REF file=composit_stand3_dropper_fix_bottom_model.FCStd obj=Join
EXTERNAL_REF file=../dropper.FCStd obj=Body
EXTERNAL_REF file=../dropper.FCStd obj=Body001

FEATURE [PartDesign::CoordinateSystem] LCS_Origin
  AttacherType = Attacher::AttachEngine3D
FEATURE [App::Link] dropper_fix_bottom
  AttachedBy = #Local_CS
  AttachedTo = Parent Assembly#LCS_Origin
  LinkedObject = -> <external composit_stand3_dropper_fix_bottom_model.FCStd>#Body
  SolverId = Asm4EE
  expr: Placement = LCS_Origin.Placement * AttachmentOffset * composit_stand3_dropper_fix_bottom_model#Local_CS.Placement ^ -1
FEATURE [App::Link] dropper_fix_top
  AttachedBy = #Local_CS
  AttachedTo = dropper_fix_bottom#Local_CS
  LinkPlacement = pos=(0,-7e-16,6) rot=(-1,0,0;3.14159rad)
  LinkedObject = -> <external composit_stand3_dropper_fix_top_model.FCStd>#Body
  Placement = pos=(0,-7e-16,6) rot=(-1,0,0;3.14159rad)
  SolverId = Asm4EE
  expr: Placement = dropper_fix_bottom.Placement * composit_stand3_dropper_fix_bottom_model#Local_CS.Placement * AttachmentOffset * composit_stand3_dropper_fix_top_model#Local_CS.Placement ^ -1
FEATURE [App::Link] dropper_fix_fixture
  AttachedBy = #Local_CS
  AttachedTo = dropper_fix_bottom#Local_CS
  LinkPlacement = pos=(50,0,0) rot=(0,0,1;0rad)
  LinkedObject = -> <external composit_stand3_dropper_fix_fixture_model.FCStd>#Body
  Placement = pos=(50,0,0) rot=(0,0,1;0rad)
  SolverId = Asm4EE
  expr: Placement = dropper_fix_bottom.Placement * composit_stand3_dropper_fix_bottom_model#Local_CS.Placement * AttachmentOffset * composit_stand3_dropper_fix_fixture_model#Local_CS.Placement ^ -1
FEATURE [App::Link] cap_outer_dropper_fix
  AttachedBy = #Local_CS
  AttachedTo = Parent Assembly#LCS_Origin
  LinkedObject = -> <external composit_stand3_dropper_fix_cap_outer_model.FCStd>#Body
  SolverId = Asm4EE
  expr: Placement = LCS_Origin.Placement * AttachmentOffset * composit_stand3_dropper_fix_cap_outer_model#Local_CS.Placement ^ -1
FEATURE [App::Link] cap_inner_1
  AttachedBy = #Local_CS
  AttachedTo = cap_outer_dropper_fix#Local_CS
  LinkedObject = -> <external composit_stand3_dropper_fix_cap_inner_model.FCStd>#Body
  SolverId = Asm4EE
  expr: Placement = cap_outer_dropper_fix.Placement * composit_stand3_dropper_fix_cap_outer_model#Local_CS.Placement * AttachmentOffset * composit_stand3_dropper_fix_cap_inner_model#Local_CS.Placement ^ -1
FEATURE [App::Link] cap_inner_2
  AttachedBy = #Local_CS001
  AttachedTo = cap_outer_dropper_fix#Local_CS
  LinkedObject = -> <external composit_stand3_dropper_fix_cap_inner_model.FCStd>#Body001
  SolverId = Asm4EE
  expr: Placement = cap_outer_dropper_fix.Placement * composit_stand3_dropper_fix_cap_outer_model#Local_CS.Placement * AttachmentOffset * composit_stand3_dropper_fix_cap_inner_model#Local_CS001.Placement ^ -1
FEATURE [App::Link] Link001  label="Join"
  LinkedObject = -> <external composit_stand3_dropper_fix_bottom_model.FCStd>#Join
FEATURE [App::Link] Link002  label="Body"
  LinkedObject = -> <external ../dropper.FCStd>#Body
FEATURE [App::Link] Link003  label="Body001"
  LinkPlacement = pos=(0,0,2.5) rot=(0,0,1;0rad)
  LinkedObject = -> <external ../dropper.FCStd>#Body001
  Placement = pos=(0,0,2.5) rot=(0,0,1;0rad)
FEATURE [Part::Compound] Compound
  Links = -> [Link002,Link003]
  Placement = pos=(0,0,4) rot=(1,0,0;3.14159rad)
FEATURE [Part::FeaturePython] Populate  label="Populate Join with dropper"  # WARN: FeaturePython — macro-defined, semantics opaque (R4)
  Copying = 0
  ExposePlacement = false
  MarkerShape = 1
  MarkerSize = 0
  NumElements = 0
  Object = -> Compound
  OutputCompounding = 1
  PlacementsTo = -> Link001
  Referencing = 0
  Type = lattice2PopulateCopies.LatticePopulateCopies
  isLattice = 0
FEATURE [PartDesign::CoordinateSystem] base_LCS
  AttacherType = Attacher::AttachEngine3D
  AttachmentSupport = -> [XY_Plane001]
FEATURE [App::Part] Part  label="droppers"
  Group = -> [Link003,Link002,Link001,Compound,Populate,base_LCS]
  Origin = -> Origin001
FEATURE [App::DocumentObjectGroup] Parts
  Group = -> [Part]
FEATURE [App::Link] droppers  label="droppers001"
  AttachedBy = #base_LCS
  AttachedTo = Parent Assembly#LCS_Origin
  LinkedObject = -> Part
  SolverId = Asm4EE
  expr: Placement = LCS_Origin.Placement * AttachmentOffset * base_LCS.Placement ^ -1
FEATURE [App::Part] Assembly
  AssemblyType = Part::Link
  Group = -> [LCS_Origin,dropper_fix_bottom,dropper_fix_top,dropper_fix_fixture,cap_outer_dropper_fix,cap_inner_1,cap_inner_2,droppers]
  Origin = -> Origin
  Type = Assembly
---- part composit_stand3_sink_assembly.FCStd = doc fcstd_7258cba6a488 ----
FCSTD DOCUMENT  (FreeCAD 1.1R38827 (Git))
Label: composit_stand3_sink_assembly
License: All rights reserved
LicenseURL: http://en.wikipedia.org/wiki/All_rights_reserved
objects: App::DocumentObjectGroup×3, App::Link×2, PartDesign::CoordinateSystem×1, App::FeaturePython×1, App::Part×1
note: 1 computed .brp shape members not serialized (recipe doc carries the construction recipe); baked Part::Feature solids carry a one-line shape summary decoded from their .brp
EXTERNAL_REF file=composit_stand3_sink_model.FCStd obj=Local_CS
EXTERNAL_REF file=composit_stand3_sink_model.FCStd obj=Body
EXTERNAL_REF file=composit_stand3_sink_hand_model.FCStd obj=Local_CS
EXTERNAL_REF file=composit_stand3_sink_model.FCStd obj=Local_CS001
EXTERNAL_REF file=composit_stand3_sink_hand_model.FCStd obj=Body

FEATURE [App::DocumentObjectGroup] Parts
FEATURE [PartDesign::CoordinateSystem] LCS_Origin
  AttacherType = Attacher::AttachEngine3D
  AttachmentSupport = -> [X_Axis]
  MapMode = 2
FEATURE [App::DocumentObjectGroup] Constraints
FEATURE [App::FeaturePython] Variables  # WARN: FeaturePython — macro-defined, semantics opaque (R4)
  Type = App::PropertyContainer
FEATURE [App::DocumentObjectGroup] Configurations
FEATURE [App::Link] sink
  AttachedBy = #Local_CS
  AttachedTo = Parent Assembly#LCS_Origin
  LinkedObject = -> <external composit_stand3_sink_model.FCStd>#Body
  SolverId = Asm4EE
  expr: Placement = LCS_Origin.Placement * AttachmentOffset * composit_stand3_sink_model#Local_CS.Placement ^ -1
FEATURE [App::Link] sink_hand
  AttachedBy = #Local_CS
  AttachedTo = sink#Local_CS001
  LinkPlacement = pos=(0.350016,0,-2.97951) rot=(0,-1,0;0.116938rad)
  LinkedObject = -> <external composit_stand3_sink_hand_model.FCStd>#Body
  Placement = pos=(0.350016,0,-2.97951) rot=(0,-1,0;0.116938rad)
  SolverId = Asm4EE
  expr: Placement = sink.Placement * composit_stand3_sink_model#Local_CS001.Placement * AttachmentOffset * composit_stand3_sink_hand_model#Local_CS.Placement ^ -1
FEATURE [App::Part] Assembly
  AssemblyType = Part::Link
  Group = -> [LCS_Origin,Constraints,Variables,Configurations,sink,sink_hand]
  Origin = -> Origin
  Type = Assembly
---- part composit_stand3_top_amplifier_model.FCStd = doc fcstd_a4cf78b27ab0 ----
FCSTD DOCUMENT  (FreeCAD 1.1R38827 (Git))
Label: composit_stand3_top_amplifier_model
License: All rights reserved
LicenseURL: http://en.wikipedia.org/wiki/All_rights_reserved
objects: PartDesign::SubShapeBinder×4, PartDesign::Pocket×4, Part::Mirroring×2, Part::FeaturePython×2, PartDesign::FeaturePython×2, Sketcher::SketchObject×2, PartDesign::Body×2, App::Link×1, PartDesign::CoordinateSystem×1, Part::Cylinder×1, Part::MultiFuse×1, PartDesign::Boolean×1, Part::Feature×1
note: 36 computed .brp shape members not serialized (recipe doc carries the construction recipe); baked Part::Feature solids carry a one-line shape summary decoded from their .brp
EXTERNAL_REF file=composit_stand3_top_amplifier_main.FCStd obj=Sketch
EXTERNAL_REF file=composit_stand3_top_amplifier_main.FCStd obj=Sketch001
EXTERNAL_REF file=composit_stand3_top_amplifier_main.FCStd obj=Join001

FEATURE [PartDesign::SubShapeBinder] Binder
  BindCopyOnChange = 0
  BindMode = 0
  ClaimChildren = false
  Fuse = false
  MakeFace = true
  OffsetFill = false
  OffsetIntersection = false
  OffsetJoinType = 0
  OffsetOpenResult = false
  PartialLoad = false
  Relative = true
  Support = -> [<external composit_stand3_top_amplifier_main.FCStd>#Sketch]
  _Version = 2
FEATURE [Part::Mirroring] Part__Mirroring  label="Binder (Mirror #1)"
  Base = (0,0,0)
  Normal = (0,1,0)
  Source = -> Binder
FEATURE [Part::FeaturePython] Connect  # WARN: FeaturePython — macro-defined, semantics opaque (R4)
  Objects = -> [Binder,Part__Mirroring]
  Tolerance = 0
FEATURE [PartDesign::SubShapeBinder] Binder001
  BindCopyOnChange = 0
  BindMode = 0
  ClaimChildren = true
  Context = -> Body [Binder001.]
  Fuse = false
  MakeFace = true
  OffsetFill = false
  OffsetIntersection = false
  OffsetJoinType = 0
  OffsetOpenResult = false
  PartialLoad = false
  Relative = false
  Support = -> [Connect]
  _Version = 2
FEATURE [PartDesign::FeaturePython] BaseBend  # WARN: FeaturePython — macro-defined, semantics opaque (R4)
  BendSide = 1
  BendSketch = -> Binder001
  MidPlane = false
  Reverse = true
  Suppressed = false
  length = 34
  radius = 2
  thickness = 2
FEATURE [Sketcher::SketchObject] Sketch
  ArcFitTolerance = 0
  AttachmentSupport = -> [XY_Plane]
  FullyConstrained = false
  MakeInternals = false
  MapMode = 5
  sketch-geometry (5):
    g0: LineSegment StartX=35.6821 StartY=-39.7187 StartZ=0 EndX=35.6821 EndY=39.7187 EndZ=0
    g1: LineSegment StartX=35.6821 StartY=39.7187 StartZ=0 EndX=-6.62185 EndY=39.7187 EndZ=0
    g2: LineSegment StartX=-6.62185 StartY=39.7187 StartZ=0 EndX=-6.62185 EndY=-39.7187 EndZ=0
    g3: LineSegment StartX=-6.62185 StartY=-39.7187 StartZ=0 EndX=35.6821 EndY=-39.7187 EndZ=0
    g4: GeomPoint [constr] X=14.5301 Y=0 Z=0
  constraints (10):
    c: Coincident(g0,g1)
    c: Coincident(g1,g2)
    c: Coincident(g2,g3)
    c: Coincident(g3,g0)
    c: Vertical(g0)
    c: Vertical(g2)
    c: Horizontal(g1)
    c: Horizontal(g3)
    c: Symmetric(g2,g0,g4)
    c: PointOnObject(g4,g-1)
FEATURE [PartDesign::Pocket] Pocket
  BaseFeature = -> BaseBend
  Direction = (0,0,-1)
  Length = 4
  Length2 = 5
  Profile = -> Sketch
  ReferenceAxis = -> Sketch [N_Axis]
  Suppressed = false
  Type = 0
  expr: Length = <<BaseBend>>.radius + <<BaseBend>>.thickness
FEATURE [PartDesign::FeaturePython] Bend  # WARN: FeaturePython — macro-defined, semantics opaque (R4)
  AutoMiter = true
  BaseFeature = -> Pocket
  BendType = 0
  LengthList = [20]
  LengthSpec = 1
  NonperforationMaxLength = 5
  Perforate = false
  PerforationAngle = 0
  PerforationInitialLength = 5
  PerforationMaxLength = 5
  ReliefFactor = 0.7
  Suppressed = false
  UseReliefFactor = false
  angle = 90
  baseObject = -> Pocket [Edge3]
  bendAList = [90]
  extend1 = 0
  extend2 = 0
  gap1 = 0
  gap2 = 0
  invert = false
  kfactor = 0.5
  length = 20
  maxExtendDist = 5
  minGap = 0.2
  minReliefGap = 1
  miterangle1 = 0
  miterangle2 = 0
  offset = 0
  radius = 2
  reliefType = 0
  reliefd = 1
  reliefw = 0.8
  sketchflip = false
  sketchinvert = false
  unfold = false
  expr: radius = BaseBend.radius
FEATURE [PartDesign::SubShapeBinder] Binder002
  BindCopyOnChange = 0
  BindMode = 0
  ClaimChildren = true
  Context = -> Body [Binder002.]
  Fuse = false
  MakeFace = true
  OffsetFill = false
  OffsetIntersection = false
  OffsetJoinType = 0
  OffsetOpenResult = false
  PartialLoad = false
  Relative = true
  Support = -> [<external composit_stand3_top_amplifier_main.FCStd>#Sketch001]
  _Version = 2
  expr: Support = composit_stand3_top_amplifier_main#Sketch001._self
FEATURE [PartDesign::Pocket] Pocket001
  BaseFeature = -> Bend
  Direction = (-0.866025,0.5,0)
  Length = 5
  Length2 = 5
  Profile = -> Binder002
  Suppressed = false
  Type = 0
FEATURE [Part::Mirroring] Part__Mirroring001  label="Binder002 (Mirror #2)"
  Base = (0,0,0)
  Normal = (0,1,0)
  Source = -> Binder002
FEATURE [PartDesign::SubShapeBinder] Binder003
  BindCopyOnChange = 0
  BindMode = 0
  ClaimChildren = false
  Context = -> Body [Binder003.]
  Fuse = false
  MakeFace = true
  OffsetFill = false
  OffsetIntersection = false
  OffsetJoinType = 0
  OffsetOpenResult = false
  PartialLoad = false
  Relative = true
  Support = -> [Part__Mirroring001]
  _Version = 2
FEATURE [PartDesign::Pocket] Pocket002
  BaseFeature = -> Pocket001
  Direction = (0.866025,0.5,0)
  Length = 5
  Length2 = 5
  Profile = -> Binder003
  Reversed = true
  Suppressed = false
  Type = 0
FEATURE [App::Link] Link  label="side_holes"
  LinkedObject = -> <external composit_stand3_top_amplifier_main.FCStd>#Join001
FEATURE [PartDesign::CoordinateSystem] Local_CS
  AttacherType = Attacher::AttachEngine3D
  AttachmentSupport = -> [XY_Plane]
  MapMode = 5
FEATURE [Part::Cylinder] Cylinder
  Angle = 360
  AttacherType = Attacher::AttachEngine3D
  FirstAngle = 0
  Height = 10
  Placement = pos=(0,0,0) rot=(1,0,0;3.14159rad)
  Radius = 1.7
  SecondAngle = 0
FEATURE [Part::FeaturePython] Populate  label="Populate side_holes with Cylinder"  # WARN: FeaturePython — macro-defined, semantics opaque (R4)
  Copying = 0
  ExposePlacement = false
  MarkerShape = 1
  MarkerSize = 0
  NumElements = 0
  Object = -> Cylinder
  OutputCompounding = 1
  PlacementsTo = -> Link
  Referencing = 0
  Type = lattice2PopulateCopies.LatticePopulateCopies
  isLattice = 0
FEATURE [PartDesign::Body] Body001
  AllowCompound = false
  Origin = -> Origin001
FEATURE [Part::MultiFuse] Fusion
  Shapes = -> [Populate]
FEATURE [PartDesign::Boolean] Boolean
  BaseFeature = -> Pocket002
  Group = -> [Fusion]
  Suppressed = false
  Type = 1
  UsePlacement = true
FEATURE [Part::Feature] Body171  label="top_amplifier_cornrer_material_0.50ansi002"
  Placement = pos=(0,0,-34) rot=(0,0,1;-1.5708rad)
  shape: bbox 29.62 x 57.09 x 34 mm, 35 faces (baked)
FEATURE [Sketcher::SketchObject] Sketch001
  ArcFitTolerance = 1e-06
  AttachmentOffset = pos=(0,0,0) rot=(0,0,1;1.0472rad)
  AttachmentSupport = -> [XY_Plane]
  FullyConstrained = true
  MakeInternals = false
  MapMode = 5
  Placement = pos=(0,0,0) rot=(0,0,1;1.0472rad)
  expr: Constraints[16] = <<Bend>>.length
  expr: Constraints[20] = <<composit_stand3_top_amplifier_main>>#<<side_Sketch>>.Constraints.length
  expr: Constraints[4] = <<BaseBend>>.radius
  sketch-geometry (8):
    g0: ArcOfCircle [constr] CenterX=1.1547 CenterY=-2 CenterZ=0 NormalX=0 NormalY=0 NormalZ=1 AngleXU=0 Radius=2 StartAngle=1.5708 EndAngle=2.61799
    g1: LineSegment [constr] StartX=-0.57735 StartY=-1 StartZ=0 EndX=0 EndY=-1e-16 EndZ=0
    g2: ArcOfCircle CenterX=4.1547 CenterY=17 CenterZ=0 NormalX=0 NormalY=0 NormalZ=1 AngleXU=0 Radius=3 StartAngle=1.5708 EndAngle=3.14159
    g3: ArcOfCircle CenterX=24 CenterY=17 CenterZ=0 NormalX=0 NormalY=0 NormalZ=1 AngleXU=0 Radius=3 StartAngle=0 EndAngle=1.5708
    g4: LineSegment StartX=1.1547 StartY=17 StartZ=0 EndX=1.1547 EndY=20 EndZ=0
    g5: LineSegment StartX=1.1547 StartY=20 StartZ=0 EndX=4.1547 EndY=20 EndZ=0
    g6: LineSegment StartX=24 StartY=20 StartZ=0 EndX=27 EndY=20 EndZ=0
    g7: LineSegment StartX=27 StartY=20 StartZ=0 EndX=27 EndY=17 EndZ=0
  constraints (21):
    c: Coincident(g1,g-1)
    c: Tangent(g1,g0) = 1.5708
    c: Tangent(g0,g-1) = 1.5708
    c: Angle(g1) = 1.0472
    c: Radius(g0) = 2
    c: Coincident(g4,g5)
    c: Coincident(g6,g7)
    c: Tangent(g2,g4) = 1.5708
    c: Tangent(g5,g2) = 1.5708
    c: Tangent(g7,g3) = 1.5708
    c: Tangent(g3,g6) = 1.5708
    c: Vertical(g7)
    c: Horizontal(g6)
    c: Vertical(g4)
    c: Horizontal(g5)
    c: Vertical(g0,g4)
    c: DistanceY(g4) = 20
    c: Equal(g2,g3)
    c: Radius(g2) = 3
    c: Horizontal(g6,g4)
    c: DistanceX(g6) = 27
FEATURE [PartDesign::Pocket] Pocket003
  BaseFeature = -> Boolean
  Direction = (0,0,-1)
  Length = 5
  Length2 = 5
  Profile = -> Sketch001
  ReferenceAxis = -> Sketch001 [N_Axis]
  Suppressed = false
  Type = 0
FEATURE [PartDesign::Body] Body  label="top_amplifier"
  AllowCompound = false
  Group = -> [Binder001,BaseBend,Sketch,Pocket,Bend,Binder002,Pocket001,Binder003,Pocket002,Local_CS,Boolean,Sketch001,Pocket003]
  Origin = -> Origin
  Tip = -> Pocket003
